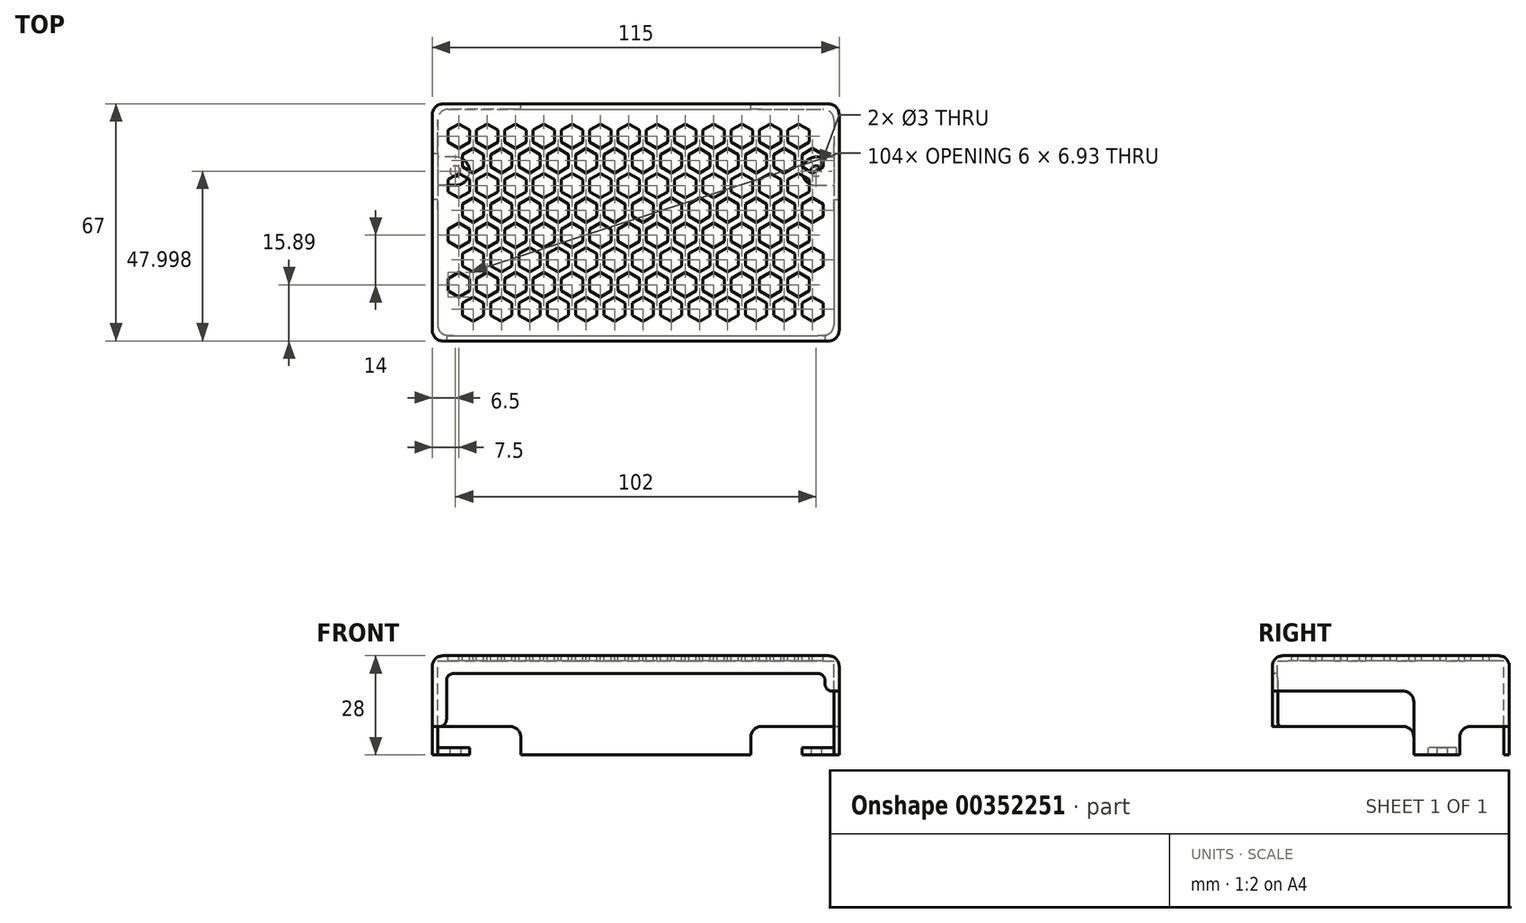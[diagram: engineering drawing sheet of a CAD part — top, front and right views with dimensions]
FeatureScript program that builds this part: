
annotation { "Feature Type Name" : "Feature", "Feature Type Description" : "" }
export const myFeature = defineFeature(function(context is Context, id is Id, definition is map)
    precondition{}
    {
        {
            var Q0;
            Q0=qCreatedBy(makeId("Top.planeOp"),FACE);
            var sketch = newSketch(context, id + "F0", { "sketchPlane" : qUnion([Q0])});
            skCircle(sketch, "E0.cCircle", {"center": v(-32, -14) * mm, "radius": 3 * mm, "construction": true});
            skLineSegment(sketch, "E0.0", {"start": v(-29, -15.73) * mm, "end": v(-32, -17.46) * mm});
            skLineSegment(sketch, "E0.1", {"start": v(-32, -17.46) * mm, "end": v(-35, -15.73) * mm});
            skLineSegment(sketch, "E0.2", {"start": v(-35, -15.73) * mm, "end": v(-35, -12.27) * mm});
            skLineSegment(sketch, "E0.3", {"start": v(-35, -12.27) * mm, "end": v(-32, -10.54) * mm});
            skLineSegment(sketch, "E0.4", {"start": v(-32, -10.54) * mm, "end": v(-29, -12.27) * mm});
            skLineSegment(sketch, "E0.5", {"start": v(-29, -12.27) * mm, "end": v(-29, -15.73) * mm});
            skPoint(sketch, "E0.0.midPoint", {"position": v(-30.5, -16.6) * mm});
            skCircle(sketch, "E1.cCircle", {"center": v(-28, -20.93) * mm, "radius": 3 * mm, "construction": true});
            skLineSegment(sketch, "E1.0", {"start": v(-25, -22.66) * mm, "end": v(-28, -24.4) * mm});
            skLineSegment(sketch, "E1.1", {"start": v(-28, -24.4) * mm, "end": v(-31, -22.66) * mm});
            skLineSegment(sketch, "E1.2", {"start": v(-31, -22.66) * mm, "end": v(-31, -19.2) * mm});
            skLineSegment(sketch, "E1.3", {"start": v(-31, -19.2) * mm, "end": v(-28, -17.46) * mm});
            skLineSegment(sketch, "E1.4", {"start": v(-28, -17.46) * mm, "end": v(-25, -19.2) * mm});
            skLineSegment(sketch, "E1.5", {"start": v(-25, -19.2) * mm, "end": v(-25, -22.66) * mm});
            skPoint(sketch, "E1.0.midPoint", {"position": v(-26.5, -23.53) * mm});
            skCircle(sketch, "E2.0.1.0", {"center": v(-28, -6.93) * mm, "radius": 3 * mm, "construction": true});
            skLineSegment(sketch, "E2.0.1.1", {"start": v(-28, -10.4) * mm, "end": v(-31, -8.66) * mm});
            skLineSegment(sketch, "E2.0.1.2", {"start": v(-31, -8.66) * mm, "end": v(-31, -5.2) * mm});
            skLineSegment(sketch, "E2.0.1.3", {"start": v(-31, -5.2) * mm, "end": v(-28, -3.46) * mm});
            skLineSegment(sketch, "E2.0.1.4", {"start": v(-28, -3.46) * mm, "end": v(-25, -5.2) * mm});
            skPoint(sketch, "E2.0.1.5", {"position": v(-26.5, -9.53) * mm});
            skPoint(sketch, "E2.0.1.6", {"position": v(-30.5, -2.6) * mm});
            skLineSegment(sketch, "E2.0.1.7", {"start": v(-25, -5.2) * mm, "end": v(-25, -8.66) * mm});
            skLineSegment(sketch, "E2.0.1.8", {"start": v(-29, 1.73) * mm, "end": v(-29, -1.73) * mm});
            skLineSegment(sketch, "E2.0.1.9", {"start": v(-32, 3.46) * mm, "end": v(-29, 1.73) * mm});
            skLineSegment(sketch, "E2.0.1.10", {"start": v(-35, 1.73) * mm, "end": v(-32, 3.46) * mm});
            skLineSegment(sketch, "E2.0.1.11", {"start": v(-35, -1.73) * mm, "end": v(-35, 1.73) * mm});
            skLineSegment(sketch, "E2.0.1.12", {"start": v(-32, -3.46) * mm, "end": v(-35, -1.73) * mm});
            skCircle(sketch, "E2.0.1.13", {"center": v(-32, 0) * mm, "radius": 3 * mm, "construction": true});
            skLineSegment(sketch, "E2.0.1.14", {"start": v(-25, -8.66) * mm, "end": v(-28, -10.4) * mm});
            skLineSegment(sketch, "E2.0.1.15", {"start": v(-29, -1.73) * mm, "end": v(-32, -3.46) * mm});
            skCircle(sketch, "E2.0.2.0", {"center": v(-28, 7.07) * mm, "radius": 3 * mm, "construction": true});
            skLineSegment(sketch, "E2.0.2.1", {"start": v(-28, 3.6) * mm, "end": v(-31, 5.34) * mm});
            skLineSegment(sketch, "E2.0.2.2", {"start": v(-31, 5.34) * mm, "end": v(-31, 8.8) * mm});
            skLineSegment(sketch, "E2.0.2.3", {"start": v(-31, 8.8) * mm, "end": v(-28, 10.54) * mm});
            skLineSegment(sketch, "E2.0.2.4", {"start": v(-28, 10.54) * mm, "end": v(-25, 8.8) * mm});
            skPoint(sketch, "E2.0.2.5", {"position": v(-26.5, 4.47) * mm});
            skPoint(sketch, "E2.0.2.6", {"position": v(-30.5, 11.4) * mm});
            skLineSegment(sketch, "E2.0.2.7", {"start": v(-25, 8.8) * mm, "end": v(-25, 5.34) * mm});
            skLineSegment(sketch, "E2.0.2.8", {"start": v(-29, 15.73) * mm, "end": v(-29, 12.27) * mm});
            skLineSegment(sketch, "E2.0.2.9", {"start": v(-32, 17.46) * mm, "end": v(-29, 15.73) * mm});
            skLineSegment(sketch, "E2.0.2.10", {"start": v(-35, 15.73) * mm, "end": v(-32, 17.46) * mm});
            skLineSegment(sketch, "E2.0.2.11", {"start": v(-35, 12.27) * mm, "end": v(-35, 15.73) * mm});
            skLineSegment(sketch, "E2.0.2.12", {"start": v(-32, 10.54) * mm, "end": v(-35, 12.27) * mm});
            skCircle(sketch, "E2.0.2.13", {"center": v(-32, 14) * mm, "radius": 3 * mm, "construction": true});
            skLineSegment(sketch, "E2.0.2.14", {"start": v(-25, 5.34) * mm, "end": v(-28, 3.6) * mm});
            skLineSegment(sketch, "E2.0.2.15", {"start": v(-29, 12.27) * mm, "end": v(-32, 10.54) * mm});
            skCircle(sketch, "E2.1.0.0", {"center": v(-20, -20.93) * mm, "radius": 3 * mm, "construction": true});
            skLineSegment(sketch, "E2.1.0.1", {"start": v(-20, -24.4) * mm, "end": v(-23, -22.66) * mm});
            skLineSegment(sketch, "E2.1.0.2", {"start": v(-23, -22.66) * mm, "end": v(-23, -19.2) * mm});
            skLineSegment(sketch, "E2.1.0.3", {"start": v(-23, -19.2) * mm, "end": v(-20, -17.46) * mm});
            skLineSegment(sketch, "E2.1.0.4", {"start": v(-20, -17.46) * mm, "end": v(-17, -19.2) * mm});
            skPoint(sketch, "E2.1.0.5", {"position": v(-18.5, -23.53) * mm});
            skPoint(sketch, "E2.1.0.6", {"position": v(-22.5, -16.6) * mm});
            skLineSegment(sketch, "E2.1.0.7", {"start": v(-17, -19.2) * mm, "end": v(-17, -22.66) * mm});
            skLineSegment(sketch, "E2.1.0.8", {"start": v(-21, -12.27) * mm, "end": v(-21, -15.73) * mm});
            skLineSegment(sketch, "E2.1.0.9", {"start": v(-24, -10.54) * mm, "end": v(-21, -12.27) * mm});
            skLineSegment(sketch, "E2.1.0.10", {"start": v(-27, -12.27) * mm, "end": v(-24, -10.54) * mm});
            skLineSegment(sketch, "E2.1.0.11", {"start": v(-27, -15.73) * mm, "end": v(-27, -12.27) * mm});
            skLineSegment(sketch, "E2.1.0.12", {"start": v(-24, -17.46) * mm, "end": v(-27, -15.73) * mm});
            skCircle(sketch, "E2.1.0.13", {"center": v(-24, -14) * mm, "radius": 3 * mm, "construction": true});
            skLineSegment(sketch, "E2.1.0.14", {"start": v(-17, -22.66) * mm, "end": v(-20, -24.4) * mm});
            skLineSegment(sketch, "E2.1.0.15", {"start": v(-21, -15.73) * mm, "end": v(-24, -17.46) * mm});
            skCircle(sketch, "E2.1.1.0", {"center": v(-20, -6.93) * mm, "radius": 3 * mm, "construction": true});
            skLineSegment(sketch, "E2.1.1.1", {"start": v(-20, -10.4) * mm, "end": v(-23, -8.66) * mm});
            skLineSegment(sketch, "E2.1.1.2", {"start": v(-23, -8.66) * mm, "end": v(-23, -5.2) * mm});
            skLineSegment(sketch, "E2.1.1.3", {"start": v(-23, -5.2) * mm, "end": v(-20, -3.46) * mm});
            skLineSegment(sketch, "E2.1.1.4", {"start": v(-20, -3.46) * mm, "end": v(-17, -5.2) * mm});
            skPoint(sketch, "E2.1.1.5", {"position": v(-18.5, -9.53) * mm});
            skPoint(sketch, "E2.1.1.6", {"position": v(-22.5, -2.6) * mm});
            skLineSegment(sketch, "E2.1.1.7", {"start": v(-17, -5.2) * mm, "end": v(-17, -8.66) * mm});
            skLineSegment(sketch, "E2.1.1.8", {"start": v(-21, 1.73) * mm, "end": v(-21, -1.73) * mm});
            skLineSegment(sketch, "E2.1.1.9", {"start": v(-24, 3.46) * mm, "end": v(-21, 1.73) * mm});
            skLineSegment(sketch, "E2.1.1.10", {"start": v(-27, 1.73) * mm, "end": v(-24, 3.46) * mm});
            skLineSegment(sketch, "E2.1.1.11", {"start": v(-27, -1.73) * mm, "end": v(-27, 1.73) * mm});
            skLineSegment(sketch, "E2.1.1.12", {"start": v(-24, -3.46) * mm, "end": v(-27, -1.73) * mm});
            skCircle(sketch, "E2.1.1.13", {"center": v(-24, 0) * mm, "radius": 3 * mm, "construction": true});
            skLineSegment(sketch, "E2.1.1.14", {"start": v(-17, -8.66) * mm, "end": v(-20, -10.4) * mm});
            skLineSegment(sketch, "E2.1.1.15", {"start": v(-21, -1.73) * mm, "end": v(-24, -3.46) * mm});
            skCircle(sketch, "E2.1.2.0", {"center": v(-20, 7.07) * mm, "radius": 3 * mm, "construction": true});
            skLineSegment(sketch, "E2.1.2.1", {"start": v(-20, 3.6) * mm, "end": v(-23, 5.34) * mm});
            skLineSegment(sketch, "E2.1.2.2", {"start": v(-23, 5.34) * mm, "end": v(-23, 8.8) * mm});
            skLineSegment(sketch, "E2.1.2.3", {"start": v(-23, 8.8) * mm, "end": v(-20, 10.54) * mm});
            skLineSegment(sketch, "E2.1.2.4", {"start": v(-20, 10.54) * mm, "end": v(-17, 8.8) * mm});
            skPoint(sketch, "E2.1.2.5", {"position": v(-18.5, 4.47) * mm});
            skPoint(sketch, "E2.1.2.6", {"position": v(-22.5, 11.4) * mm});
            skLineSegment(sketch, "E2.1.2.7", {"start": v(-17, 8.8) * mm, "end": v(-17, 5.34) * mm});
            skLineSegment(sketch, "E2.1.2.8", {"start": v(-21, 15.73) * mm, "end": v(-21, 12.27) * mm});
            skLineSegment(sketch, "E2.1.2.9", {"start": v(-24, 17.46) * mm, "end": v(-21, 15.73) * mm});
            skLineSegment(sketch, "E2.1.2.10", {"start": v(-27, 15.73) * mm, "end": v(-24, 17.46) * mm});
            skLineSegment(sketch, "E2.1.2.11", {"start": v(-27, 12.27) * mm, "end": v(-27, 15.73) * mm});
            skLineSegment(sketch, "E2.1.2.12", {"start": v(-24, 10.54) * mm, "end": v(-27, 12.27) * mm});
            skCircle(sketch, "E2.1.2.13", {"center": v(-24, 14) * mm, "radius": 3 * mm, "construction": true});
            skLineSegment(sketch, "E2.1.2.14", {"start": v(-17, 5.34) * mm, "end": v(-20, 3.6) * mm});
            skLineSegment(sketch, "E2.1.2.15", {"start": v(-21, 12.27) * mm, "end": v(-24, 10.54) * mm});
            skCircle(sketch, "E2.2.0.0", {"center": v(-12, -20.93) * mm, "radius": 3 * mm, "construction": true});
            skLineSegment(sketch, "E2.2.0.1", {"start": v(-12, -24.4) * mm, "end": v(-15, -22.66) * mm});
            skLineSegment(sketch, "E2.2.0.2", {"start": v(-15, -22.66) * mm, "end": v(-15, -19.2) * mm});
            skLineSegment(sketch, "E2.2.0.3", {"start": v(-15, -19.2) * mm, "end": v(-12, -17.46) * mm});
            skLineSegment(sketch, "E2.2.0.4", {"start": v(-12, -17.46) * mm, "end": v(-9, -19.2) * mm});
            skPoint(sketch, "E2.2.0.5", {"position": v(-10.5, -23.53) * mm});
            skPoint(sketch, "E2.2.0.6", {"position": v(-14.5, -16.6) * mm});
            skLineSegment(sketch, "E2.2.0.7", {"start": v(-9, -19.2) * mm, "end": v(-9, -22.66) * mm});
            skLineSegment(sketch, "E2.2.0.8", {"start": v(-13, -12.27) * mm, "end": v(-13, -15.73) * mm});
            skLineSegment(sketch, "E2.2.0.9", {"start": v(-16, -10.54) * mm, "end": v(-13, -12.27) * mm});
            skLineSegment(sketch, "E2.2.0.10", {"start": v(-19, -12.27) * mm, "end": v(-16, -10.54) * mm});
            skLineSegment(sketch, "E2.2.0.11", {"start": v(-19, -15.73) * mm, "end": v(-19, -12.27) * mm});
            skLineSegment(sketch, "E2.2.0.12", {"start": v(-16, -17.46) * mm, "end": v(-19, -15.73) * mm});
            skCircle(sketch, "E2.2.0.13", {"center": v(-16, -14) * mm, "radius": 3 * mm, "construction": true});
            skLineSegment(sketch, "E2.2.0.14", {"start": v(-9, -22.66) * mm, "end": v(-12, -24.4) * mm});
            skLineSegment(sketch, "E2.2.0.15", {"start": v(-13, -15.73) * mm, "end": v(-16, -17.46) * mm});
            skCircle(sketch, "E2.2.1.0", {"center": v(-12, -6.93) * mm, "radius": 3 * mm, "construction": true});
            skLineSegment(sketch, "E2.2.1.1", {"start": v(-12, -10.4) * mm, "end": v(-15, -8.66) * mm});
            skLineSegment(sketch, "E2.2.1.2", {"start": v(-15, -8.66) * mm, "end": v(-15, -5.2) * mm});
            skLineSegment(sketch, "E2.2.1.3", {"start": v(-15, -5.2) * mm, "end": v(-12, -3.46) * mm});
            skLineSegment(sketch, "E2.2.1.4", {"start": v(-12, -3.46) * mm, "end": v(-9, -5.2) * mm});
            skPoint(sketch, "E2.2.1.5", {"position": v(-10.5, -9.53) * mm});
            skPoint(sketch, "E2.2.1.6", {"position": v(-14.5, -2.6) * mm});
            skLineSegment(sketch, "E2.2.1.7", {"start": v(-9, -5.2) * mm, "end": v(-9, -8.66) * mm});
            skLineSegment(sketch, "E2.2.1.8", {"start": v(-13, 1.73) * mm, "end": v(-13, -1.73) * mm});
            skLineSegment(sketch, "E2.2.1.9", {"start": v(-16, 3.46) * mm, "end": v(-13, 1.73) * mm});
            skLineSegment(sketch, "E2.2.1.10", {"start": v(-19, 1.73) * mm, "end": v(-16, 3.46) * mm});
            skLineSegment(sketch, "E2.2.1.11", {"start": v(-19, -1.73) * mm, "end": v(-19, 1.73) * mm});
            skLineSegment(sketch, "E2.2.1.12", {"start": v(-16, -3.46) * mm, "end": v(-19, -1.73) * mm});
            skCircle(sketch, "E2.2.1.13", {"center": v(-16, 0) * mm, "radius": 3 * mm, "construction": true});
            skLineSegment(sketch, "E2.2.1.14", {"start": v(-9, -8.66) * mm, "end": v(-12, -10.4) * mm});
            skLineSegment(sketch, "E2.2.1.15", {"start": v(-13, -1.73) * mm, "end": v(-16, -3.46) * mm});
            skCircle(sketch, "E2.2.2.0", {"center": v(-12, 7.07) * mm, "radius": 3 * mm, "construction": true});
            skLineSegment(sketch, "E2.2.2.1", {"start": v(-12, 3.6) * mm, "end": v(-15, 5.34) * mm});
            skLineSegment(sketch, "E2.2.2.2", {"start": v(-15, 5.34) * mm, "end": v(-15, 8.8) * mm});
            skLineSegment(sketch, "E2.2.2.3", {"start": v(-15, 8.8) * mm, "end": v(-12, 10.54) * mm});
            skLineSegment(sketch, "E2.2.2.4", {"start": v(-12, 10.54) * mm, "end": v(-9, 8.8) * mm});
            skPoint(sketch, "E2.2.2.5", {"position": v(-10.5, 4.47) * mm});
            skPoint(sketch, "E2.2.2.6", {"position": v(-14.5, 11.4) * mm});
            skLineSegment(sketch, "E2.2.2.7", {"start": v(-9, 8.8) * mm, "end": v(-9, 5.34) * mm});
            skLineSegment(sketch, "E2.2.2.8", {"start": v(-13, 15.73) * mm, "end": v(-13, 12.27) * mm});
            skLineSegment(sketch, "E2.2.2.9", {"start": v(-16, 17.46) * mm, "end": v(-13, 15.73) * mm});
            skLineSegment(sketch, "E2.2.2.10", {"start": v(-19, 15.73) * mm, "end": v(-16, 17.46) * mm});
            skLineSegment(sketch, "E2.2.2.11", {"start": v(-19, 12.27) * mm, "end": v(-19, 15.73) * mm});
            skLineSegment(sketch, "E2.2.2.12", {"start": v(-16, 10.54) * mm, "end": v(-19, 12.27) * mm});
            skCircle(sketch, "E2.2.2.13", {"center": v(-16, 14) * mm, "radius": 3 * mm, "construction": true});
            skLineSegment(sketch, "E2.2.2.14", {"start": v(-9, 5.34) * mm, "end": v(-12, 3.6) * mm});
            skLineSegment(sketch, "E2.2.2.15", {"start": v(-13, 12.27) * mm, "end": v(-16, 10.54) * mm});
            skCircle(sketch, "E2.3.0.0", {"center": v(-4, -20.93) * mm, "radius": 3 * mm, "construction": true});
            skLineSegment(sketch, "E2.3.0.1", {"start": v(-4, -24.4) * mm, "end": v(-7, -22.66) * mm});
            skLineSegment(sketch, "E2.3.0.2", {"start": v(-7, -22.66) * mm, "end": v(-7, -19.2) * mm});
            skLineSegment(sketch, "E2.3.0.3", {"start": v(-7, -19.2) * mm, "end": v(-4, -17.46) * mm});
            skLineSegment(sketch, "E2.3.0.4", {"start": v(-4, -17.46) * mm, "end": v(-1, -19.2) * mm});
            skPoint(sketch, "E2.3.0.5", {"position": v(-2.5, -23.53) * mm});
            skPoint(sketch, "E2.3.0.6", {"position": v(-6.5, -16.6) * mm});
            skLineSegment(sketch, "E2.3.0.7", {"start": v(-1, -19.2) * mm, "end": v(-1, -22.66) * mm});
            skLineSegment(sketch, "E2.3.0.8", {"start": v(-5, -12.27) * mm, "end": v(-5, -15.73) * mm});
            skLineSegment(sketch, "E2.3.0.9", {"start": v(-8, -10.54) * mm, "end": v(-5, -12.27) * mm});
            skLineSegment(sketch, "E2.3.0.10", {"start": v(-11, -12.27) * mm, "end": v(-8, -10.54) * mm});
            skLineSegment(sketch, "E2.3.0.11", {"start": v(-11, -15.73) * mm, "end": v(-11, -12.27) * mm});
            skLineSegment(sketch, "E2.3.0.12", {"start": v(-8, -17.46) * mm, "end": v(-11, -15.73) * mm});
            skCircle(sketch, "E2.3.0.13", {"center": v(-8, -14) * mm, "radius": 3 * mm, "construction": true});
            skLineSegment(sketch, "E2.3.0.14", {"start": v(-1, -22.66) * mm, "end": v(-4, -24.4) * mm});
            skLineSegment(sketch, "E2.3.0.15", {"start": v(-5, -15.73) * mm, "end": v(-8, -17.46) * mm});
            skCircle(sketch, "E2.3.1.0", {"center": v(-4, -6.93) * mm, "radius": 3 * mm, "construction": true});
            skLineSegment(sketch, "E2.3.1.1", {"start": v(-4, -10.4) * mm, "end": v(-7, -8.66) * mm});
            skLineSegment(sketch, "E2.3.1.2", {"start": v(-7, -8.66) * mm, "end": v(-7, -5.2) * mm});
            skLineSegment(sketch, "E2.3.1.3", {"start": v(-7, -5.2) * mm, "end": v(-4, -3.46) * mm});
            skLineSegment(sketch, "E2.3.1.4", {"start": v(-4, -3.46) * mm, "end": v(-1, -5.2) * mm});
            skPoint(sketch, "E2.3.1.5", {"position": v(-2.5, -9.53) * mm});
            skPoint(sketch, "E2.3.1.6", {"position": v(-6.5, -2.6) * mm});
            skLineSegment(sketch, "E2.3.1.7", {"start": v(-1, -5.2) * mm, "end": v(-1, -8.66) * mm});
            skLineSegment(sketch, "E2.3.1.8", {"start": v(-5, 1.73) * mm, "end": v(-5, -1.73) * mm});
            skLineSegment(sketch, "E2.3.1.9", {"start": v(-8, 3.46) * mm, "end": v(-5, 1.73) * mm});
            skLineSegment(sketch, "E2.3.1.10", {"start": v(-11, 1.73) * mm, "end": v(-8, 3.46) * mm});
            skLineSegment(sketch, "E2.3.1.11", {"start": v(-11, -1.73) * mm, "end": v(-11, 1.73) * mm});
            skLineSegment(sketch, "E2.3.1.12", {"start": v(-8, -3.46) * mm, "end": v(-11, -1.73) * mm});
            skCircle(sketch, "E2.3.1.13", {"center": v(-8, 0) * mm, "radius": 3 * mm, "construction": true});
            skLineSegment(sketch, "E2.3.1.14", {"start": v(-1, -8.66) * mm, "end": v(-4, -10.4) * mm});
            skLineSegment(sketch, "E2.3.1.15", {"start": v(-5, -1.73) * mm, "end": v(-8, -3.46) * mm});
            skCircle(sketch, "E2.3.2.0", {"center": v(-4, 7.07) * mm, "radius": 3 * mm, "construction": true});
            skLineSegment(sketch, "E2.3.2.1", {"start": v(-4, 3.6) * mm, "end": v(-7, 5.34) * mm});
            skLineSegment(sketch, "E2.3.2.2", {"start": v(-7, 5.34) * mm, "end": v(-7, 8.8) * mm});
            skLineSegment(sketch, "E2.3.2.3", {"start": v(-7, 8.8) * mm, "end": v(-4, 10.54) * mm});
            skLineSegment(sketch, "E2.3.2.4", {"start": v(-4, 10.54) * mm, "end": v(-1, 8.8) * mm});
            skPoint(sketch, "E2.3.2.5", {"position": v(-2.5, 4.47) * mm});
            skPoint(sketch, "E2.3.2.6", {"position": v(-6.5, 11.4) * mm});
            skLineSegment(sketch, "E2.3.2.7", {"start": v(-1, 8.8) * mm, "end": v(-1, 5.34) * mm});
            skLineSegment(sketch, "E2.3.2.8", {"start": v(-5, 15.73) * mm, "end": v(-5, 12.27) * mm});
            skLineSegment(sketch, "E2.3.2.9", {"start": v(-8, 17.46) * mm, "end": v(-5, 15.73) * mm});
            skLineSegment(sketch, "E2.3.2.10", {"start": v(-11, 15.73) * mm, "end": v(-8, 17.46) * mm});
            skLineSegment(sketch, "E2.3.2.11", {"start": v(-11, 12.27) * mm, "end": v(-11, 15.73) * mm});
            skLineSegment(sketch, "E2.3.2.12", {"start": v(-8, 10.54) * mm, "end": v(-11, 12.27) * mm});
            skCircle(sketch, "E2.3.2.13", {"center": v(-8, 14) * mm, "radius": 3 * mm, "construction": true});
            skLineSegment(sketch, "E2.3.2.14", {"start": v(-1, 5.34) * mm, "end": v(-4, 3.6) * mm});
            skLineSegment(sketch, "E2.3.2.15", {"start": v(-5, 12.27) * mm, "end": v(-8, 10.54) * mm});
            skCircle(sketch, "E2.4.0.0", {"center": v(4, -20.93) * mm, "radius": 3 * mm, "construction": true});
            skLineSegment(sketch, "E2.4.0.1", {"start": v(4, -24.4) * mm, "end": v(1, -22.66) * mm});
            skLineSegment(sketch, "E2.4.0.2", {"start": v(1, -22.66) * mm, "end": v(1, -19.2) * mm});
            skLineSegment(sketch, "E2.4.0.3", {"start": v(1, -19.2) * mm, "end": v(4, -17.46) * mm});
            skLineSegment(sketch, "E2.4.0.4", {"start": v(4, -17.46) * mm, "end": v(7, -19.2) * mm});
            skPoint(sketch, "E2.4.0.5", {"position": v(5.5, -23.53) * mm});
            skPoint(sketch, "E2.4.0.6", {"position": v(1.5, -16.6) * mm});
            skLineSegment(sketch, "E2.4.0.7", {"start": v(7, -19.2) * mm, "end": v(7, -22.66) * mm});
            skLineSegment(sketch, "E2.4.0.8", {"start": v(3, -12.27) * mm, "end": v(3, -15.73) * mm});
            skLineSegment(sketch, "E2.4.0.9", {"start": v(0, -10.54) * mm, "end": v(3, -12.27) * mm});
            skLineSegment(sketch, "E2.4.0.10", {"start": v(-3, -12.27) * mm, "end": v(0, -10.54) * mm});
            skLineSegment(sketch, "E2.4.0.11", {"start": v(-3, -15.73) * mm, "end": v(-3, -12.27) * mm});
            skLineSegment(sketch, "E2.4.0.12", {"start": v(0, -17.46) * mm, "end": v(-3, -15.73) * mm});
            skCircle(sketch, "E2.4.0.13", {"center": v(0, -14) * mm, "radius": 3 * mm, "construction": true});
            skLineSegment(sketch, "E2.4.0.14", {"start": v(7, -22.66) * mm, "end": v(4, -24.4) * mm});
            skLineSegment(sketch, "E2.4.0.15", {"start": v(3, -15.73) * mm, "end": v(0, -17.46) * mm});
            skCircle(sketch, "E2.4.1.0", {"center": v(4, -6.93) * mm, "radius": 3 * mm, "construction": true});
            skLineSegment(sketch, "E2.4.1.1", {"start": v(4, -10.4) * mm, "end": v(1, -8.66) * mm});
            skLineSegment(sketch, "E2.4.1.2", {"start": v(1, -8.66) * mm, "end": v(1, -5.2) * mm});
            skLineSegment(sketch, "E2.4.1.3", {"start": v(1, -5.2) * mm, "end": v(4, -3.46) * mm});
            skLineSegment(sketch, "E2.4.1.4", {"start": v(4, -3.46) * mm, "end": v(7, -5.2) * mm});
            skPoint(sketch, "E2.4.1.5", {"position": v(5.5, -9.53) * mm});
            skPoint(sketch, "E2.4.1.6", {"position": v(1.5, -2.6) * mm});
            skLineSegment(sketch, "E2.4.1.7", {"start": v(7, -5.2) * mm, "end": v(7, -8.66) * mm});
            skLineSegment(sketch, "E2.4.1.8", {"start": v(3, 1.73) * mm, "end": v(3, -1.73) * mm});
            skLineSegment(sketch, "E2.4.1.9", {"start": v(0, 3.46) * mm, "end": v(3, 1.73) * mm});
            skLineSegment(sketch, "E2.4.1.10", {"start": v(-3, 1.73) * mm, "end": v(0, 3.46) * mm});
            skLineSegment(sketch, "E2.4.1.11", {"start": v(-3, -1.73) * mm, "end": v(-3, 1.73) * mm});
            skLineSegment(sketch, "E2.4.1.12", {"start": v(0, -3.46) * mm, "end": v(-3, -1.73) * mm});
            skCircle(sketch, "E2.4.1.13", {"center": v(0, 0) * mm, "radius": 3 * mm, "construction": true});
            skLineSegment(sketch, "E2.4.1.14", {"start": v(7, -8.66) * mm, "end": v(4, -10.4) * mm});
            skLineSegment(sketch, "E2.4.1.15", {"start": v(3, -1.73) * mm, "end": v(0, -3.46) * mm});
            skCircle(sketch, "E2.4.2.0", {"center": v(4, 7.07) * mm, "radius": 3 * mm, "construction": true});
            skLineSegment(sketch, "E2.4.2.1", {"start": v(4, 3.6) * mm, "end": v(1, 5.34) * mm});
            skLineSegment(sketch, "E2.4.2.2", {"start": v(1, 5.34) * mm, "end": v(1, 8.8) * mm});
            skLineSegment(sketch, "E2.4.2.3", {"start": v(1, 8.8) * mm, "end": v(4, 10.54) * mm});
            skLineSegment(sketch, "E2.4.2.4", {"start": v(4, 10.54) * mm, "end": v(7, 8.8) * mm});
            skPoint(sketch, "E2.4.2.5", {"position": v(5.5, 4.47) * mm});
            skPoint(sketch, "E2.4.2.6", {"position": v(1.5, 11.4) * mm});
            skLineSegment(sketch, "E2.4.2.7", {"start": v(7, 8.8) * mm, "end": v(7, 5.34) * mm});
            skLineSegment(sketch, "E2.4.2.8", {"start": v(3, 15.73) * mm, "end": v(3, 12.27) * mm});
            skLineSegment(sketch, "E2.4.2.9", {"start": v(0, 17.46) * mm, "end": v(3, 15.73) * mm});
            skLineSegment(sketch, "E2.4.2.10", {"start": v(-3, 15.73) * mm, "end": v(0, 17.46) * mm});
            skLineSegment(sketch, "E2.4.2.11", {"start": v(-3, 12.27) * mm, "end": v(-3, 15.73) * mm});
            skLineSegment(sketch, "E2.4.2.12", {"start": v(0, 10.54) * mm, "end": v(-3, 12.27) * mm});
            skCircle(sketch, "E2.4.2.13", {"center": v(0, 14) * mm, "radius": 3 * mm, "construction": true});
            skLineSegment(sketch, "E2.4.2.14", {"start": v(7, 5.34) * mm, "end": v(4, 3.6) * mm});
            skLineSegment(sketch, "E2.4.2.15", {"start": v(3, 12.27) * mm, "end": v(0, 10.54) * mm});
            skCircle(sketch, "E2.5.0.0", {"center": v(12, -20.93) * mm, "radius": 3 * mm, "construction": true});
            skLineSegment(sketch, "E2.5.0.1", {"start": v(12, -24.4) * mm, "end": v(9, -22.66) * mm});
            skLineSegment(sketch, "E2.5.0.2", {"start": v(9, -22.66) * mm, "end": v(9, -19.2) * mm});
            skLineSegment(sketch, "E2.5.0.3", {"start": v(9, -19.2) * mm, "end": v(12, -17.46) * mm});
            skLineSegment(sketch, "E2.5.0.4", {"start": v(12, -17.46) * mm, "end": v(15, -19.2) * mm});
            skPoint(sketch, "E2.5.0.5", {"position": v(13.5, -23.53) * mm});
            skPoint(sketch, "E2.5.0.6", {"position": v(9.5, -16.6) * mm});
            skLineSegment(sketch, "E2.5.0.7", {"start": v(15, -19.2) * mm, "end": v(15, -22.66) * mm});
            skLineSegment(sketch, "E2.5.0.8", {"start": v(11, -12.27) * mm, "end": v(11, -15.73) * mm});
            skLineSegment(sketch, "E2.5.0.9", {"start": v(8, -10.54) * mm, "end": v(11, -12.27) * mm});
            skLineSegment(sketch, "E2.5.0.10", {"start": v(5, -12.27) * mm, "end": v(8, -10.54) * mm});
            skLineSegment(sketch, "E2.5.0.11", {"start": v(5, -15.73) * mm, "end": v(5, -12.27) * mm});
            skLineSegment(sketch, "E2.5.0.12", {"start": v(8, -17.46) * mm, "end": v(5, -15.73) * mm});
            skCircle(sketch, "E2.5.0.13", {"center": v(8, -14) * mm, "radius": 3 * mm, "construction": true});
            skLineSegment(sketch, "E2.5.0.14", {"start": v(15, -22.66) * mm, "end": v(12, -24.4) * mm});
            skLineSegment(sketch, "E2.5.0.15", {"start": v(11, -15.73) * mm, "end": v(8, -17.46) * mm});
            skCircle(sketch, "E2.5.1.0", {"center": v(12, -6.93) * mm, "radius": 3 * mm, "construction": true});
            skLineSegment(sketch, "E2.5.1.1", {"start": v(12, -10.4) * mm, "end": v(9, -8.66) * mm});
            skLineSegment(sketch, "E2.5.1.2", {"start": v(9, -8.66) * mm, "end": v(9, -5.2) * mm});
            skLineSegment(sketch, "E2.5.1.3", {"start": v(9, -5.2) * mm, "end": v(12, -3.46) * mm});
            skLineSegment(sketch, "E2.5.1.4", {"start": v(12, -3.46) * mm, "end": v(15, -5.2) * mm});
            skPoint(sketch, "E2.5.1.5", {"position": v(13.5, -9.53) * mm});
            skPoint(sketch, "E2.5.1.6", {"position": v(9.5, -2.6) * mm});
            skLineSegment(sketch, "E2.5.1.7", {"start": v(15, -5.2) * mm, "end": v(15, -8.66) * mm});
            skLineSegment(sketch, "E2.5.1.8", {"start": v(11, 1.73) * mm, "end": v(11, -1.73) * mm});
            skLineSegment(sketch, "E2.5.1.9", {"start": v(8, 3.46) * mm, "end": v(11, 1.73) * mm});
            skLineSegment(sketch, "E2.5.1.10", {"start": v(5, 1.73) * mm, "end": v(8, 3.46) * mm});
            skLineSegment(sketch, "E2.5.1.11", {"start": v(5, -1.73) * mm, "end": v(5, 1.73) * mm});
            skLineSegment(sketch, "E2.5.1.12", {"start": v(8, -3.46) * mm, "end": v(5, -1.73) * mm});
            skCircle(sketch, "E2.5.1.13", {"center": v(8, 0) * mm, "radius": 3 * mm, "construction": true});
            skLineSegment(sketch, "E2.5.1.14", {"start": v(15, -8.66) * mm, "end": v(12, -10.4) * mm});
            skLineSegment(sketch, "E2.5.1.15", {"start": v(11, -1.73) * mm, "end": v(8, -3.46) * mm});
            skCircle(sketch, "E2.5.2.0", {"center": v(12, 7.07) * mm, "radius": 3 * mm, "construction": true});
            skLineSegment(sketch, "E2.5.2.1", {"start": v(12, 3.6) * mm, "end": v(9, 5.34) * mm});
            skLineSegment(sketch, "E2.5.2.2", {"start": v(9, 5.34) * mm, "end": v(9, 8.8) * mm});
            skLineSegment(sketch, "E2.5.2.3", {"start": v(9, 8.8) * mm, "end": v(12, 10.54) * mm});
            skLineSegment(sketch, "E2.5.2.4", {"start": v(12, 10.54) * mm, "end": v(15, 8.8) * mm});
            skPoint(sketch, "E2.5.2.5", {"position": v(13.5, 4.47) * mm});
            skPoint(sketch, "E2.5.2.6", {"position": v(9.5, 11.4) * mm});
            skLineSegment(sketch, "E2.5.2.7", {"start": v(15, 8.8) * mm, "end": v(15, 5.34) * mm});
            skLineSegment(sketch, "E2.5.2.8", {"start": v(11, 15.73) * mm, "end": v(11, 12.27) * mm});
            skLineSegment(sketch, "E2.5.2.9", {"start": v(8, 17.46) * mm, "end": v(11, 15.73) * mm});
            skLineSegment(sketch, "E2.5.2.10", {"start": v(5, 15.73) * mm, "end": v(8, 17.46) * mm});
            skLineSegment(sketch, "E2.5.2.11", {"start": v(5, 12.27) * mm, "end": v(5, 15.73) * mm});
            skLineSegment(sketch, "E2.5.2.12", {"start": v(8, 10.54) * mm, "end": v(5, 12.27) * mm});
            skCircle(sketch, "E2.5.2.13", {"center": v(8, 14) * mm, "radius": 3 * mm, "construction": true});
            skLineSegment(sketch, "E2.5.2.14", {"start": v(15, 5.34) * mm, "end": v(12, 3.6) * mm});
            skLineSegment(sketch, "E2.5.2.15", {"start": v(11, 12.27) * mm, "end": v(8, 10.54) * mm});
            skCircle(sketch, "E2.6.0.0", {"center": v(20, -20.93) * mm, "radius": 3 * mm, "construction": true});
            skLineSegment(sketch, "E2.6.0.1", {"start": v(20, -24.4) * mm, "end": v(17, -22.66) * mm});
            skLineSegment(sketch, "E2.6.0.2", {"start": v(17, -22.66) * mm, "end": v(17, -19.2) * mm});
            skLineSegment(sketch, "E2.6.0.3", {"start": v(17, -19.2) * mm, "end": v(20, -17.46) * mm});
            skLineSegment(sketch, "E2.6.0.4", {"start": v(20, -17.46) * mm, "end": v(23, -19.2) * mm});
            skPoint(sketch, "E2.6.0.5", {"position": v(21.5, -23.53) * mm});
            skPoint(sketch, "E2.6.0.6", {"position": v(17.5, -16.6) * mm});
            skLineSegment(sketch, "E2.6.0.7", {"start": v(23, -19.2) * mm, "end": v(23, -22.66) * mm});
            skLineSegment(sketch, "E2.6.0.8", {"start": v(19, -12.27) * mm, "end": v(19, -15.73) * mm});
            skLineSegment(sketch, "E2.6.0.9", {"start": v(16, -10.54) * mm, "end": v(19, -12.27) * mm});
            skLineSegment(sketch, "E2.6.0.10", {"start": v(13, -12.27) * mm, "end": v(16, -10.54) * mm});
            skLineSegment(sketch, "E2.6.0.11", {"start": v(13, -15.73) * mm, "end": v(13, -12.27) * mm});
            skLineSegment(sketch, "E2.6.0.12", {"start": v(16, -17.46) * mm, "end": v(13, -15.73) * mm});
            skCircle(sketch, "E2.6.0.13", {"center": v(16, -14) * mm, "radius": 3 * mm, "construction": true});
            skLineSegment(sketch, "E2.6.0.14", {"start": v(23, -22.66) * mm, "end": v(20, -24.4) * mm});
            skLineSegment(sketch, "E2.6.0.15", {"start": v(19, -15.73) * mm, "end": v(16, -17.46) * mm});
            skCircle(sketch, "E2.6.1.0", {"center": v(20, -6.93) * mm, "radius": 3 * mm, "construction": true});
            skLineSegment(sketch, "E2.6.1.1", {"start": v(20, -10.4) * mm, "end": v(17, -8.66) * mm});
            skLineSegment(sketch, "E2.6.1.2", {"start": v(17, -8.66) * mm, "end": v(17, -5.2) * mm});
            skLineSegment(sketch, "E2.6.1.3", {"start": v(17, -5.2) * mm, "end": v(20, -3.46) * mm});
            skLineSegment(sketch, "E2.6.1.4", {"start": v(20, -3.46) * mm, "end": v(23, -5.2) * mm});
            skPoint(sketch, "E2.6.1.5", {"position": v(21.5, -9.53) * mm});
            skPoint(sketch, "E2.6.1.6", {"position": v(17.5, -2.6) * mm});
            skLineSegment(sketch, "E2.6.1.7", {"start": v(23, -5.2) * mm, "end": v(23, -8.66) * mm});
            skLineSegment(sketch, "E2.6.1.8", {"start": v(19, 1.73) * mm, "end": v(19, -1.73) * mm});
            skLineSegment(sketch, "E2.6.1.9", {"start": v(16, 3.46) * mm, "end": v(19, 1.73) * mm});
            skLineSegment(sketch, "E2.6.1.10", {"start": v(13, 1.73) * mm, "end": v(16, 3.46) * mm});
            skLineSegment(sketch, "E2.6.1.11", {"start": v(13, -1.73) * mm, "end": v(13, 1.73) * mm});
            skLineSegment(sketch, "E2.6.1.12", {"start": v(16, -3.46) * mm, "end": v(13, -1.73) * mm});
            skCircle(sketch, "E2.6.1.13", {"center": v(16, 0) * mm, "radius": 3 * mm, "construction": true});
            skLineSegment(sketch, "E2.6.1.14", {"start": v(23, -8.66) * mm, "end": v(20, -10.4) * mm});
            skLineSegment(sketch, "E2.6.1.15", {"start": v(19, -1.73) * mm, "end": v(16, -3.46) * mm});
            skCircle(sketch, "E2.6.2.0", {"center": v(20, 7.07) * mm, "radius": 3 * mm, "construction": true});
            skLineSegment(sketch, "E2.6.2.1", {"start": v(20, 3.6) * mm, "end": v(17, 5.34) * mm});
            skLineSegment(sketch, "E2.6.2.2", {"start": v(17, 5.34) * mm, "end": v(17, 8.8) * mm});
            skLineSegment(sketch, "E2.6.2.3", {"start": v(17, 8.8) * mm, "end": v(20, 10.54) * mm});
            skLineSegment(sketch, "E2.6.2.4", {"start": v(20, 10.54) * mm, "end": v(23, 8.8) * mm});
            skPoint(sketch, "E2.6.2.5", {"position": v(21.5, 4.47) * mm});
            skPoint(sketch, "E2.6.2.6", {"position": v(17.5, 11.4) * mm});
            skLineSegment(sketch, "E2.6.2.7", {"start": v(23, 8.8) * mm, "end": v(23, 5.34) * mm});
            skLineSegment(sketch, "E2.6.2.8", {"start": v(19, 15.73) * mm, "end": v(19, 12.27) * mm});
            skLineSegment(sketch, "E2.6.2.9", {"start": v(16, 17.46) * mm, "end": v(19, 15.73) * mm});
            skLineSegment(sketch, "E2.6.2.10", {"start": v(13, 15.73) * mm, "end": v(16, 17.46) * mm});
            skLineSegment(sketch, "E2.6.2.11", {"start": v(13, 12.27) * mm, "end": v(13, 15.73) * mm});
            skLineSegment(sketch, "E2.6.2.12", {"start": v(16, 10.54) * mm, "end": v(13, 12.27) * mm});
            skCircle(sketch, "E2.6.2.13", {"center": v(16, 14) * mm, "radius": 3 * mm, "construction": true});
            skLineSegment(sketch, "E2.6.2.14", {"start": v(23, 5.34) * mm, "end": v(20, 3.6) * mm});
            skLineSegment(sketch, "E2.6.2.15", {"start": v(19, 12.27) * mm, "end": v(16, 10.54) * mm});
            skCircle(sketch, "E2.7.0.0", {"center": v(28, -20.93) * mm, "radius": 3 * mm, "construction": true});
            skLineSegment(sketch, "E2.7.0.1", {"start": v(28, -24.4) * mm, "end": v(25, -22.66) * mm});
            skLineSegment(sketch, "E2.7.0.2", {"start": v(25, -22.66) * mm, "end": v(25, -19.2) * mm});
            skLineSegment(sketch, "E2.7.0.3", {"start": v(25, -19.2) * mm, "end": v(28, -17.46) * mm});
            skLineSegment(sketch, "E2.7.0.4", {"start": v(28, -17.46) * mm, "end": v(31, -19.2) * mm});
            skPoint(sketch, "E2.7.0.5", {"position": v(29.5, -23.53) * mm});
            skPoint(sketch, "E2.7.0.6", {"position": v(25.5, -16.6) * mm});
            skLineSegment(sketch, "E2.7.0.7", {"start": v(31, -19.2) * mm, "end": v(31, -22.66) * mm});
            skLineSegment(sketch, "E2.7.0.8", {"start": v(27, -12.27) * mm, "end": v(27, -15.73) * mm});
            skLineSegment(sketch, "E2.7.0.9", {"start": v(24, -10.54) * mm, "end": v(27, -12.27) * mm});
            skLineSegment(sketch, "E2.7.0.10", {"start": v(21, -12.27) * mm, "end": v(24, -10.54) * mm});
            skLineSegment(sketch, "E2.7.0.11", {"start": v(21, -15.73) * mm, "end": v(21, -12.27) * mm});
            skLineSegment(sketch, "E2.7.0.12", {"start": v(24, -17.46) * mm, "end": v(21, -15.73) * mm});
            skCircle(sketch, "E2.7.0.13", {"center": v(24, -14) * mm, "radius": 3 * mm, "construction": true});
            skLineSegment(sketch, "E2.7.0.14", {"start": v(31, -22.66) * mm, "end": v(28, -24.4) * mm});
            skLineSegment(sketch, "E2.7.0.15", {"start": v(27, -15.73) * mm, "end": v(24, -17.46) * mm});
            skCircle(sketch, "E2.7.1.0", {"center": v(28, -6.93) * mm, "radius": 3 * mm, "construction": true});
            skLineSegment(sketch, "E2.7.1.1", {"start": v(28, -10.4) * mm, "end": v(25, -8.66) * mm});
            skLineSegment(sketch, "E2.7.1.2", {"start": v(25, -8.66) * mm, "end": v(25, -5.2) * mm});
            skLineSegment(sketch, "E2.7.1.3", {"start": v(25, -5.2) * mm, "end": v(28, -3.46) * mm});
            skLineSegment(sketch, "E2.7.1.4", {"start": v(28, -3.46) * mm, "end": v(31, -5.2) * mm});
            skPoint(sketch, "E2.7.1.5", {"position": v(29.5, -9.53) * mm});
            skPoint(sketch, "E2.7.1.6", {"position": v(25.5, -2.6) * mm});
            skLineSegment(sketch, "E2.7.1.7", {"start": v(31, -5.2) * mm, "end": v(31, -8.66) * mm});
            skLineSegment(sketch, "E2.7.1.8", {"start": v(27, 1.73) * mm, "end": v(27, -1.73) * mm});
            skLineSegment(sketch, "E2.7.1.9", {"start": v(24, 3.46) * mm, "end": v(27, 1.73) * mm});
            skLineSegment(sketch, "E2.7.1.10", {"start": v(21, 1.73) * mm, "end": v(24, 3.46) * mm});
            skLineSegment(sketch, "E2.7.1.11", {"start": v(21, -1.73) * mm, "end": v(21, 1.73) * mm});
            skLineSegment(sketch, "E2.7.1.12", {"start": v(24, -3.46) * mm, "end": v(21, -1.73) * mm});
            skCircle(sketch, "E2.7.1.13", {"center": v(24, 0) * mm, "radius": 3 * mm, "construction": true});
            skLineSegment(sketch, "E2.7.1.14", {"start": v(31, -8.66) * mm, "end": v(28, -10.4) * mm});
            skLineSegment(sketch, "E2.7.1.15", {"start": v(27, -1.73) * mm, "end": v(24, -3.46) * mm});
            skCircle(sketch, "E2.7.2.0", {"center": v(28, 7.07) * mm, "radius": 3 * mm, "construction": true});
            skLineSegment(sketch, "E2.7.2.1", {"start": v(28, 3.6) * mm, "end": v(25, 5.34) * mm});
            skLineSegment(sketch, "E2.7.2.2", {"start": v(25, 5.34) * mm, "end": v(25, 8.8) * mm});
            skLineSegment(sketch, "E2.7.2.3", {"start": v(25, 8.8) * mm, "end": v(28, 10.54) * mm});
            skLineSegment(sketch, "E2.7.2.4", {"start": v(28, 10.54) * mm, "end": v(31, 8.8) * mm});
            skPoint(sketch, "E2.7.2.5", {"position": v(29.5, 4.47) * mm});
            skPoint(sketch, "E2.7.2.6", {"position": v(25.5, 11.4) * mm});
            skLineSegment(sketch, "E2.7.2.7", {"start": v(31, 8.8) * mm, "end": v(31, 5.34) * mm});
            skLineSegment(sketch, "E2.7.2.8", {"start": v(27, 15.73) * mm, "end": v(27, 12.27) * mm});
            skLineSegment(sketch, "E2.7.2.9", {"start": v(24, 17.46) * mm, "end": v(27, 15.73) * mm});
            skLineSegment(sketch, "E2.7.2.10", {"start": v(21, 15.73) * mm, "end": v(24, 17.46) * mm});
            skLineSegment(sketch, "E2.7.2.11", {"start": v(21, 12.27) * mm, "end": v(21, 15.73) * mm});
            skLineSegment(sketch, "E2.7.2.12", {"start": v(24, 10.54) * mm, "end": v(21, 12.27) * mm});
            skCircle(sketch, "E2.7.2.13", {"center": v(24, 14) * mm, "radius": 3 * mm, "construction": true});
            skLineSegment(sketch, "E2.7.2.14", {"start": v(31, 5.34) * mm, "end": v(28, 3.6) * mm});
            skLineSegment(sketch, "E2.7.2.15", {"start": v(27, 12.27) * mm, "end": v(24, 10.54) * mm});
            skLineSegment(sketch, "E2.direction1", {"start": v(-31, -22.66) * mm, "end": v(-23, -22.66) * mm, "construction": true});
            skLineSegment(sketch, "E2.direction2", {"start": v(-31, -22.66) * mm, "end": v(-31, -8.66) * mm, "construction": true});
            skLineSegment(sketch, "E3.bottom", {"start": v(-38, 35.6) * mm, "end": v(74, 35.6) * mm});
            skLineSegment(sketch, "E3.top", {"start": v(-38, -28.4) * mm, "end": v(74, -28.4) * mm});
            skLineSegment(sketch, "E3.left", {"start": v(-38, 35.6) * mm, "end": v(-38, -28.4) * mm});
            skLineSegment(sketch, "E3.right", {"start": v(74, 35.6) * mm, "end": v(74, -28.4) * mm});
            skCircle(sketch, "E4.0.8.0", {"center": v(36, -20.93) * mm, "radius": 3 * mm, "construction": true});
            skLineSegment(sketch, "E4.2.8.0", {"start": v(36, -24.4) * mm, "end": v(33, -22.66) * mm});
            skLineSegment(sketch, "E4.5.8.0", {"start": v(33, -22.66) * mm, "end": v(33, -19.2) * mm});
            skLineSegment(sketch, "E4.8.8.0", {"start": v(33, -19.2) * mm, "end": v(36, -17.46) * mm});
            skLineSegment(sketch, "E4.11.8.0", {"start": v(36, -17.46) * mm, "end": v(39, -19.2) * mm});
            skPoint(sketch, "E4.14.8.0", {"position": v(37.5, -23.53) * mm});
            skPoint(sketch, "E4.15.8.0", {"position": v(33.5, -16.6) * mm});
            skLineSegment(sketch, "E4.16.8.0", {"start": v(39, -19.2) * mm, "end": v(39, -22.66) * mm});
            skLineSegment(sketch, "E4.19.8.0", {"start": v(35, -12.27) * mm, "end": v(35, -15.73) * mm});
            skLineSegment(sketch, "E4.22.8.0", {"start": v(32, -10.54) * mm, "end": v(35, -12.27) * mm});
            skLineSegment(sketch, "E4.25.8.0", {"start": v(29, -12.27) * mm, "end": v(32, -10.54) * mm});
            skLineSegment(sketch, "E4.28.8.0", {"start": v(29, -15.73) * mm, "end": v(29, -12.27) * mm});
            skLineSegment(sketch, "E4.31.8.0", {"start": v(32, -17.46) * mm, "end": v(29, -15.73) * mm});
            skCircle(sketch, "E4.34.8.0", {"center": v(32, -14) * mm, "radius": 3 * mm, "construction": true});
            skLineSegment(sketch, "E4.36.8.0", {"start": v(39, -22.66) * mm, "end": v(36, -24.4) * mm});
            skLineSegment(sketch, "E4.39.8.0", {"start": v(35, -15.73) * mm, "end": v(32, -17.46) * mm});
            skCircle(sketch, "E4.0.8.1", {"center": v(36, -6.93) * mm, "radius": 3 * mm, "construction": true});
            skLineSegment(sketch, "E4.2.8.1", {"start": v(36, -10.4) * mm, "end": v(33, -8.66) * mm});
            skLineSegment(sketch, "E4.5.8.1", {"start": v(33, -8.66) * mm, "end": v(33, -5.2) * mm});
            skLineSegment(sketch, "E4.8.8.1", {"start": v(33, -5.2) * mm, "end": v(36, -3.46) * mm});
            skLineSegment(sketch, "E4.11.8.1", {"start": v(36, -3.46) * mm, "end": v(39, -5.2) * mm});
            skPoint(sketch, "E4.14.8.1", {"position": v(37.5, -9.53) * mm});
            skPoint(sketch, "E4.15.8.1", {"position": v(33.5, -2.6) * mm});
            skLineSegment(sketch, "E4.16.8.1", {"start": v(39, -5.2) * mm, "end": v(39, -8.66) * mm});
            skLineSegment(sketch, "E4.19.8.1", {"start": v(35, 1.73) * mm, "end": v(35, -1.73) * mm});
            skLineSegment(sketch, "E4.22.8.1", {"start": v(32, 3.46) * mm, "end": v(35, 1.73) * mm});
            skLineSegment(sketch, "E4.25.8.1", {"start": v(29, 1.73) * mm, "end": v(32, 3.46) * mm});
            skLineSegment(sketch, "E4.28.8.1", {"start": v(29, -1.73) * mm, "end": v(29, 1.73) * mm});
            skLineSegment(sketch, "E4.31.8.1", {"start": v(32, -3.46) * mm, "end": v(29, -1.73) * mm});
            skCircle(sketch, "E4.34.8.1", {"center": v(32, 0) * mm, "radius": 3 * mm, "construction": true});
            skLineSegment(sketch, "E4.36.8.1", {"start": v(39, -8.66) * mm, "end": v(36, -10.4) * mm});
            skLineSegment(sketch, "E4.39.8.1", {"start": v(35, -1.73) * mm, "end": v(32, -3.46) * mm});
            skCircle(sketch, "E4.0.8.2", {"center": v(36, 7.07) * mm, "radius": 3 * mm, "construction": true});
            skLineSegment(sketch, "E4.2.8.2", {"start": v(36, 3.6) * mm, "end": v(33, 5.34) * mm});
            skLineSegment(sketch, "E4.5.8.2", {"start": v(33, 5.34) * mm, "end": v(33, 8.8) * mm});
            skLineSegment(sketch, "E4.8.8.2", {"start": v(33, 8.8) * mm, "end": v(36, 10.54) * mm});
            skLineSegment(sketch, "E4.11.8.2", {"start": v(36, 10.54) * mm, "end": v(39, 8.8) * mm});
            skPoint(sketch, "E4.14.8.2", {"position": v(37.5, 4.47) * mm});
            skPoint(sketch, "E4.15.8.2", {"position": v(33.5, 11.4) * mm});
            skLineSegment(sketch, "E4.16.8.2", {"start": v(39, 8.8) * mm, "end": v(39, 5.34) * mm});
            skLineSegment(sketch, "E4.19.8.2", {"start": v(35, 15.73) * mm, "end": v(35, 12.27) * mm});
            skLineSegment(sketch, "E4.22.8.2", {"start": v(32, 17.46) * mm, "end": v(35, 15.73) * mm});
            skLineSegment(sketch, "E4.25.8.2", {"start": v(29, 15.73) * mm, "end": v(32, 17.46) * mm});
            skLineSegment(sketch, "E4.28.8.2", {"start": v(29, 12.27) * mm, "end": v(29, 15.73) * mm});
            skLineSegment(sketch, "E4.31.8.2", {"start": v(32, 10.54) * mm, "end": v(29, 12.27) * mm});
            skCircle(sketch, "E4.34.8.2", {"center": v(32, 14) * mm, "radius": 3 * mm, "construction": true});
            skLineSegment(sketch, "E4.36.8.2", {"start": v(39, 5.34) * mm, "end": v(36, 3.6) * mm});
            skLineSegment(sketch, "E4.39.8.2", {"start": v(35, 12.27) * mm, "end": v(32, 10.54) * mm});
            skCircle(sketch, "E4.0.9.0", {"center": v(44, -20.93) * mm, "radius": 3 * mm, "construction": true});
            skLineSegment(sketch, "E4.2.9.0", {"start": v(44, -24.4) * mm, "end": v(41, -22.66) * mm});
            skLineSegment(sketch, "E4.5.9.0", {"start": v(41, -22.66) * mm, "end": v(41, -19.2) * mm});
            skLineSegment(sketch, "E4.8.9.0", {"start": v(41, -19.2) * mm, "end": v(44, -17.46) * mm});
            skLineSegment(sketch, "E4.11.9.0", {"start": v(44, -17.46) * mm, "end": v(47, -19.2) * mm});
            skPoint(sketch, "E4.14.9.0", {"position": v(45.5, -23.53) * mm});
            skPoint(sketch, "E4.15.9.0", {"position": v(41.5, -16.6) * mm});
            skLineSegment(sketch, "E4.16.9.0", {"start": v(47, -19.2) * mm, "end": v(47, -22.66) * mm});
            skLineSegment(sketch, "E4.19.9.0", {"start": v(43, -12.27) * mm, "end": v(43, -15.73) * mm});
            skLineSegment(sketch, "E4.22.9.0", {"start": v(40, -10.54) * mm, "end": v(43, -12.27) * mm});
            skLineSegment(sketch, "E4.25.9.0", {"start": v(37, -12.27) * mm, "end": v(40, -10.54) * mm});
            skLineSegment(sketch, "E4.28.9.0", {"start": v(37, -15.73) * mm, "end": v(37, -12.27) * mm});
            skLineSegment(sketch, "E4.31.9.0", {"start": v(40, -17.46) * mm, "end": v(37, -15.73) * mm});
            skCircle(sketch, "E4.34.9.0", {"center": v(40, -14) * mm, "radius": 3 * mm, "construction": true});
            skLineSegment(sketch, "E4.36.9.0", {"start": v(47, -22.66) * mm, "end": v(44, -24.4) * mm});
            skLineSegment(sketch, "E4.39.9.0", {"start": v(43, -15.73) * mm, "end": v(40, -17.46) * mm});
            skCircle(sketch, "E4.0.9.1", {"center": v(44, -6.93) * mm, "radius": 3 * mm, "construction": true});
            skLineSegment(sketch, "E4.2.9.1", {"start": v(44, -10.4) * mm, "end": v(41, -8.66) * mm});
            skLineSegment(sketch, "E4.5.9.1", {"start": v(41, -8.66) * mm, "end": v(41, -5.2) * mm});
            skLineSegment(sketch, "E4.8.9.1", {"start": v(41, -5.2) * mm, "end": v(44, -3.46) * mm});
            skLineSegment(sketch, "E4.11.9.1", {"start": v(44, -3.46) * mm, "end": v(47, -5.2) * mm});
            skPoint(sketch, "E4.14.9.1", {"position": v(45.5, -9.53) * mm});
            skPoint(sketch, "E4.15.9.1", {"position": v(41.5, -2.6) * mm});
            skLineSegment(sketch, "E4.16.9.1", {"start": v(47, -5.2) * mm, "end": v(47, -8.66) * mm});
            skLineSegment(sketch, "E4.19.9.1", {"start": v(43, 1.73) * mm, "end": v(43, -1.73) * mm});
            skLineSegment(sketch, "E4.22.9.1", {"start": v(40, 3.46) * mm, "end": v(43, 1.73) * mm});
            skLineSegment(sketch, "E4.25.9.1", {"start": v(37, 1.73) * mm, "end": v(40, 3.46) * mm});
            skLineSegment(sketch, "E4.28.9.1", {"start": v(37, -1.73) * mm, "end": v(37, 1.73) * mm});
            skLineSegment(sketch, "E4.31.9.1", {"start": v(40, -3.46) * mm, "end": v(37, -1.73) * mm});
            skCircle(sketch, "E4.34.9.1", {"center": v(40, 0) * mm, "radius": 3 * mm, "construction": true});
            skLineSegment(sketch, "E4.36.9.1", {"start": v(47, -8.66) * mm, "end": v(44, -10.4) * mm});
            skLineSegment(sketch, "E4.39.9.1", {"start": v(43, -1.73) * mm, "end": v(40, -3.46) * mm});
            skCircle(sketch, "E4.0.9.2", {"center": v(44, 7.07) * mm, "radius": 3 * mm, "construction": true});
            skLineSegment(sketch, "E4.2.9.2", {"start": v(44, 3.6) * mm, "end": v(41, 5.34) * mm});
            skLineSegment(sketch, "E4.5.9.2", {"start": v(41, 5.34) * mm, "end": v(41, 8.8) * mm});
            skLineSegment(sketch, "E4.8.9.2", {"start": v(41, 8.8) * mm, "end": v(44, 10.54) * mm});
            skLineSegment(sketch, "E4.11.9.2", {"start": v(44, 10.54) * mm, "end": v(47, 8.8) * mm});
            skPoint(sketch, "E4.14.9.2", {"position": v(45.5, 4.47) * mm});
            skPoint(sketch, "E4.15.9.2", {"position": v(41.5, 11.4) * mm});
            skLineSegment(sketch, "E4.16.9.2", {"start": v(47, 8.8) * mm, "end": v(47, 5.34) * mm});
            skLineSegment(sketch, "E4.19.9.2", {"start": v(43, 15.73) * mm, "end": v(43, 12.27) * mm});
            skLineSegment(sketch, "E4.22.9.2", {"start": v(40, 17.46) * mm, "end": v(43, 15.73) * mm});
            skLineSegment(sketch, "E4.25.9.2", {"start": v(37, 15.73) * mm, "end": v(40, 17.46) * mm});
            skLineSegment(sketch, "E4.28.9.2", {"start": v(37, 12.27) * mm, "end": v(37, 15.73) * mm});
            skLineSegment(sketch, "E4.31.9.2", {"start": v(40, 10.54) * mm, "end": v(37, 12.27) * mm});
            skCircle(sketch, "E4.34.9.2", {"center": v(40, 14) * mm, "radius": 3 * mm, "construction": true});
            skLineSegment(sketch, "E4.36.9.2", {"start": v(47, 5.34) * mm, "end": v(44, 3.6) * mm});
            skLineSegment(sketch, "E4.39.9.2", {"start": v(43, 12.27) * mm, "end": v(40, 10.54) * mm});
            skCircle(sketch, "E5.0.10.0", {"center": v(52, -20.93) * mm, "radius": 3 * mm, "construction": true});
            skLineSegment(sketch, "E5.2.10.0", {"start": v(52, -24.4) * mm, "end": v(49, -22.66) * mm});
            skLineSegment(sketch, "E5.5.10.0", {"start": v(49, -22.66) * mm, "end": v(49, -19.2) * mm});
            skLineSegment(sketch, "E5.8.10.0", {"start": v(49, -19.2) * mm, "end": v(52, -17.46) * mm});
            skLineSegment(sketch, "E5.11.10.0", {"start": v(52, -17.46) * mm, "end": v(55, -19.2) * mm});
            skPoint(sketch, "E5.14.10.0", {"position": v(53.5, -23.53) * mm});
            skPoint(sketch, "E5.15.10.0", {"position": v(49.5, -16.6) * mm});
            skLineSegment(sketch, "E5.16.10.0", {"start": v(55, -19.2) * mm, "end": v(55, -22.66) * mm});
            skLineSegment(sketch, "E5.19.10.0", {"start": v(51, -12.27) * mm, "end": v(51, -15.73) * mm});
            skLineSegment(sketch, "E5.22.10.0", {"start": v(48, -10.54) * mm, "end": v(51, -12.27) * mm});
            skLineSegment(sketch, "E5.25.10.0", {"start": v(45, -12.27) * mm, "end": v(48, -10.54) * mm});
            skLineSegment(sketch, "E5.28.10.0", {"start": v(45, -15.73) * mm, "end": v(45, -12.27) * mm});
            skLineSegment(sketch, "E5.31.10.0", {"start": v(48, -17.46) * mm, "end": v(45, -15.73) * mm});
            skCircle(sketch, "E5.34.10.0", {"center": v(48, -14) * mm, "radius": 3 * mm, "construction": true});
            skLineSegment(sketch, "E5.36.10.0", {"start": v(55, -22.66) * mm, "end": v(52, -24.4) * mm});
            skLineSegment(sketch, "E5.39.10.0", {"start": v(51, -15.73) * mm, "end": v(48, -17.46) * mm});
            skCircle(sketch, "E5.0.10.1", {"center": v(52, -6.93) * mm, "radius": 3 * mm, "construction": true});
            skLineSegment(sketch, "E5.2.10.1", {"start": v(52, -10.4) * mm, "end": v(49, -8.66) * mm});
            skLineSegment(sketch, "E5.5.10.1", {"start": v(49, -8.66) * mm, "end": v(49, -5.2) * mm});
            skLineSegment(sketch, "E5.8.10.1", {"start": v(49, -5.2) * mm, "end": v(52, -3.46) * mm});
            skLineSegment(sketch, "E5.11.10.1", {"start": v(52, -3.46) * mm, "end": v(55, -5.2) * mm});
            skPoint(sketch, "E5.14.10.1", {"position": v(53.5, -9.53) * mm});
            skPoint(sketch, "E5.15.10.1", {"position": v(49.5, -2.6) * mm});
            skLineSegment(sketch, "E5.16.10.1", {"start": v(55, -5.2) * mm, "end": v(55, -8.66) * mm});
            skLineSegment(sketch, "E5.19.10.1", {"start": v(51, 1.73) * mm, "end": v(51, -1.73) * mm});
            skLineSegment(sketch, "E5.22.10.1", {"start": v(48, 3.46) * mm, "end": v(51, 1.73) * mm});
            skLineSegment(sketch, "E5.25.10.1", {"start": v(45, 1.73) * mm, "end": v(48, 3.46) * mm});
            skLineSegment(sketch, "E5.28.10.1", {"start": v(45, -1.73) * mm, "end": v(45, 1.73) * mm});
            skLineSegment(sketch, "E5.31.10.1", {"start": v(48, -3.46) * mm, "end": v(45, -1.73) * mm});
            skCircle(sketch, "E5.34.10.1", {"center": v(48, 0) * mm, "radius": 3 * mm, "construction": true});
            skLineSegment(sketch, "E5.36.10.1", {"start": v(55, -8.66) * mm, "end": v(52, -10.4) * mm});
            skLineSegment(sketch, "E5.39.10.1", {"start": v(51, -1.73) * mm, "end": v(48, -3.46) * mm});
            skCircle(sketch, "E5.0.10.2", {"center": v(52, 7.07) * mm, "radius": 3 * mm, "construction": true});
            skLineSegment(sketch, "E5.2.10.2", {"start": v(52, 3.6) * mm, "end": v(49, 5.34) * mm});
            skLineSegment(sketch, "E5.5.10.2", {"start": v(49, 5.34) * mm, "end": v(49, 8.8) * mm});
            skLineSegment(sketch, "E5.8.10.2", {"start": v(49, 8.8) * mm, "end": v(52, 10.54) * mm});
            skLineSegment(sketch, "E5.11.10.2", {"start": v(52, 10.54) * mm, "end": v(55, 8.8) * mm});
            skPoint(sketch, "E5.14.10.2", {"position": v(53.5, 4.47) * mm});
            skPoint(sketch, "E5.15.10.2", {"position": v(49.5, 11.4) * mm});
            skLineSegment(sketch, "E5.16.10.2", {"start": v(55, 8.8) * mm, "end": v(55, 5.34) * mm});
            skLineSegment(sketch, "E5.19.10.2", {"start": v(51, 15.73) * mm, "end": v(51, 12.27) * mm});
            skLineSegment(sketch, "E5.22.10.2", {"start": v(48, 17.46) * mm, "end": v(51, 15.73) * mm});
            skLineSegment(sketch, "E5.25.10.2", {"start": v(45, 15.73) * mm, "end": v(48, 17.46) * mm});
            skLineSegment(sketch, "E5.28.10.2", {"start": v(45, 12.27) * mm, "end": v(45, 15.73) * mm});
            skLineSegment(sketch, "E5.31.10.2", {"start": v(48, 10.54) * mm, "end": v(45, 12.27) * mm});
            skCircle(sketch, "E5.34.10.2", {"center": v(48, 14) * mm, "radius": 3 * mm, "construction": true});
            skLineSegment(sketch, "E5.36.10.2", {"start": v(55, 5.34) * mm, "end": v(52, 3.6) * mm});
            skLineSegment(sketch, "E5.39.10.2", {"start": v(51, 12.27) * mm, "end": v(48, 10.54) * mm});
            skLineSegment(sketch, "E6.bottom", {"start": v(-39.5, 37.1) * mm, "end": v(75.5, 37.1) * mm});
            skLineSegment(sketch, "E6.top", {"start": v(-39.5, -29.9) * mm, "end": v(75.5, -29.9) * mm});
            skLineSegment(sketch, "E6.left", {"start": v(-39.5, 37.1) * mm, "end": v(-39.5, -29.9) * mm});
            skLineSegment(sketch, "E6.right", {"start": v(75.5, 37.1) * mm, "end": v(75.5, -29.9) * mm});
            skCircle(sketch, "E7.0.11.0", {"center": v(60, -20.93) * mm, "radius": 3 * mm, "construction": true});
            skLineSegment(sketch, "E7.2.11.0", {"start": v(60, -24.4) * mm, "end": v(57, -22.66) * mm});
            skLineSegment(sketch, "E7.5.11.0", {"start": v(57, -22.66) * mm, "end": v(57, -19.2) * mm});
            skLineSegment(sketch, "E7.8.11.0", {"start": v(57, -19.2) * mm, "end": v(60, -17.46) * mm});
            skLineSegment(sketch, "E7.11.11.0", {"start": v(60, -17.46) * mm, "end": v(63, -19.2) * mm});
            skPoint(sketch, "E7.14.11.0", {"position": v(61.5, -23.53) * mm});
            skPoint(sketch, "E7.15.11.0", {"position": v(57.5, -16.6) * mm});
            skLineSegment(sketch, "E7.16.11.0", {"start": v(63, -19.2) * mm, "end": v(63, -22.66) * mm});
            skLineSegment(sketch, "E7.19.11.0", {"start": v(59, -12.27) * mm, "end": v(59, -15.73) * mm});
            skLineSegment(sketch, "E7.22.11.0", {"start": v(56, -10.54) * mm, "end": v(59, -12.27) * mm});
            skLineSegment(sketch, "E7.25.11.0", {"start": v(53, -12.27) * mm, "end": v(56, -10.54) * mm});
            skLineSegment(sketch, "E7.28.11.0", {"start": v(53, -15.73) * mm, "end": v(53, -12.27) * mm});
            skLineSegment(sketch, "E7.31.11.0", {"start": v(56, -17.46) * mm, "end": v(53, -15.73) * mm});
            skCircle(sketch, "E7.34.11.0", {"center": v(56, -14) * mm, "radius": 3 * mm, "construction": true});
            skLineSegment(sketch, "E7.36.11.0", {"start": v(63, -22.66) * mm, "end": v(60, -24.4) * mm});
            skLineSegment(sketch, "E7.39.11.0", {"start": v(59, -15.73) * mm, "end": v(56, -17.46) * mm});
            skCircle(sketch, "E7.0.11.1", {"center": v(60, -6.93) * mm, "radius": 3 * mm, "construction": true});
            skLineSegment(sketch, "E7.2.11.1", {"start": v(60, -10.4) * mm, "end": v(57, -8.66) * mm});
            skLineSegment(sketch, "E7.5.11.1", {"start": v(57, -8.66) * mm, "end": v(57, -5.2) * mm});
            skLineSegment(sketch, "E7.8.11.1", {"start": v(57, -5.2) * mm, "end": v(60, -3.46) * mm});
            skLineSegment(sketch, "E7.11.11.1", {"start": v(60, -3.46) * mm, "end": v(63, -5.2) * mm});
            skPoint(sketch, "E7.14.11.1", {"position": v(61.5, -9.53) * mm});
            skPoint(sketch, "E7.15.11.1", {"position": v(57.5, -2.6) * mm});
            skLineSegment(sketch, "E7.16.11.1", {"start": v(63, -5.2) * mm, "end": v(63, -8.66) * mm});
            skLineSegment(sketch, "E7.19.11.1", {"start": v(59, 1.73) * mm, "end": v(59, -1.73) * mm});
            skLineSegment(sketch, "E7.22.11.1", {"start": v(56, 3.46) * mm, "end": v(59, 1.73) * mm});
            skLineSegment(sketch, "E7.25.11.1", {"start": v(53, 1.73) * mm, "end": v(56, 3.46) * mm});
            skLineSegment(sketch, "E7.28.11.1", {"start": v(53, -1.73) * mm, "end": v(53, 1.73) * mm});
            skLineSegment(sketch, "E7.31.11.1", {"start": v(56, -3.46) * mm, "end": v(53, -1.73) * mm});
            skCircle(sketch, "E7.34.11.1", {"center": v(56, 0) * mm, "radius": 3 * mm, "construction": true});
            skLineSegment(sketch, "E7.36.11.1", {"start": v(63, -8.66) * mm, "end": v(60, -10.4) * mm});
            skLineSegment(sketch, "E7.39.11.1", {"start": v(59, -1.73) * mm, "end": v(56, -3.46) * mm});
            skCircle(sketch, "E7.0.11.2", {"center": v(60, 7.07) * mm, "radius": 3 * mm, "construction": true});
            skLineSegment(sketch, "E7.2.11.2", {"start": v(60, 3.6) * mm, "end": v(57, 5.34) * mm});
            skLineSegment(sketch, "E7.5.11.2", {"start": v(57, 5.34) * mm, "end": v(57, 8.8) * mm});
            skLineSegment(sketch, "E7.8.11.2", {"start": v(57, 8.8) * mm, "end": v(60, 10.54) * mm});
            skLineSegment(sketch, "E7.11.11.2", {"start": v(60, 10.54) * mm, "end": v(63, 8.8) * mm});
            skPoint(sketch, "E7.14.11.2", {"position": v(61.5, 4.47) * mm});
            skPoint(sketch, "E7.15.11.2", {"position": v(57.5, 11.4) * mm});
            skLineSegment(sketch, "E7.16.11.2", {"start": v(63, 8.8) * mm, "end": v(63, 5.34) * mm});
            skLineSegment(sketch, "E7.19.11.2", {"start": v(59, 15.73) * mm, "end": v(59, 12.27) * mm});
            skLineSegment(sketch, "E7.22.11.2", {"start": v(56, 17.46) * mm, "end": v(59, 15.73) * mm});
            skLineSegment(sketch, "E7.25.11.2", {"start": v(53, 15.73) * mm, "end": v(56, 17.46) * mm});
            skLineSegment(sketch, "E7.28.11.2", {"start": v(53, 12.27) * mm, "end": v(53, 15.73) * mm});
            skLineSegment(sketch, "E7.31.11.2", {"start": v(56, 10.54) * mm, "end": v(53, 12.27) * mm});
            skCircle(sketch, "E7.34.11.2", {"center": v(56, 14) * mm, "radius": 3 * mm, "construction": true});
            skLineSegment(sketch, "E7.36.11.2", {"start": v(63, 5.34) * mm, "end": v(60, 3.6) * mm});
            skLineSegment(sketch, "E7.39.11.2", {"start": v(59, 12.27) * mm, "end": v(56, 10.54) * mm});
            skCircle(sketch, "E8.0.12.0", {"center": v(68, -20.93) * mm, "radius": 3 * mm, "construction": true});
            skLineSegment(sketch, "E8.2.12.0", {"start": v(68, -24.4) * mm, "end": v(65, -22.66) * mm});
            skLineSegment(sketch, "E8.5.12.0", {"start": v(65, -22.66) * mm, "end": v(65, -19.2) * mm});
            skLineSegment(sketch, "E8.8.12.0", {"start": v(65, -19.2) * mm, "end": v(68, -17.46) * mm});
            skLineSegment(sketch, "E8.11.12.0", {"start": v(68, -17.46) * mm, "end": v(71, -19.2) * mm});
            skPoint(sketch, "E8.14.12.0", {"position": v(69.5, -23.53) * mm});
            skPoint(sketch, "E8.15.12.0", {"position": v(65.5, -16.6) * mm});
            skLineSegment(sketch, "E8.16.12.0", {"start": v(71, -19.2) * mm, "end": v(71, -22.66) * mm});
            skLineSegment(sketch, "E8.19.12.0", {"start": v(67, -12.27) * mm, "end": v(67, -15.73) * mm});
            skLineSegment(sketch, "E8.22.12.0", {"start": v(64, -10.54) * mm, "end": v(67, -12.27) * mm});
            skLineSegment(sketch, "E8.25.12.0", {"start": v(61, -12.27) * mm, "end": v(64, -10.54) * mm});
            skLineSegment(sketch, "E8.28.12.0", {"start": v(61, -15.73) * mm, "end": v(61, -12.27) * mm});
            skLineSegment(sketch, "E8.31.12.0", {"start": v(64, -17.46) * mm, "end": v(61, -15.73) * mm});
            skCircle(sketch, "E8.34.12.0", {"center": v(64, -14) * mm, "radius": 3 * mm, "construction": true});
            skLineSegment(sketch, "E8.36.12.0", {"start": v(71, -22.66) * mm, "end": v(68, -24.4) * mm});
            skLineSegment(sketch, "E8.39.12.0", {"start": v(67, -15.73) * mm, "end": v(64, -17.46) * mm});
            skCircle(sketch, "E8.0.12.1", {"center": v(68, -6.93) * mm, "radius": 3 * mm, "construction": true});
            skLineSegment(sketch, "E8.2.12.1", {"start": v(68, -10.4) * mm, "end": v(65, -8.66) * mm});
            skLineSegment(sketch, "E8.5.12.1", {"start": v(65, -8.66) * mm, "end": v(65, -5.2) * mm});
            skLineSegment(sketch, "E8.8.12.1", {"start": v(65, -5.2) * mm, "end": v(68, -3.46) * mm});
            skLineSegment(sketch, "E8.11.12.1", {"start": v(68, -3.46) * mm, "end": v(71, -5.2) * mm});
            skPoint(sketch, "E8.14.12.1", {"position": v(69.5, -9.53) * mm});
            skPoint(sketch, "E8.15.12.1", {"position": v(65.5, -2.6) * mm});
            skLineSegment(sketch, "E8.16.12.1", {"start": v(71, -5.2) * mm, "end": v(71, -8.66) * mm});
            skLineSegment(sketch, "E8.19.12.1", {"start": v(67, 1.73) * mm, "end": v(67, -1.73) * mm});
            skLineSegment(sketch, "E8.22.12.1", {"start": v(64, 3.46) * mm, "end": v(67, 1.73) * mm});
            skLineSegment(sketch, "E8.25.12.1", {"start": v(61, 1.73) * mm, "end": v(64, 3.46) * mm});
            skLineSegment(sketch, "E8.28.12.1", {"start": v(61, -1.73) * mm, "end": v(61, 1.73) * mm});
            skLineSegment(sketch, "E8.31.12.1", {"start": v(64, -3.46) * mm, "end": v(61, -1.73) * mm});
            skCircle(sketch, "E8.34.12.1", {"center": v(64, 0) * mm, "radius": 3 * mm, "construction": true});
            skLineSegment(sketch, "E8.36.12.1", {"start": v(71, -8.66) * mm, "end": v(68, -10.4) * mm});
            skLineSegment(sketch, "E8.39.12.1", {"start": v(67, -1.73) * mm, "end": v(64, -3.46) * mm});
            skCircle(sketch, "E8.0.12.2", {"center": v(68, 7.07) * mm, "radius": 3 * mm, "construction": true});
            skLineSegment(sketch, "E8.2.12.2", {"start": v(68, 3.6) * mm, "end": v(65, 5.34) * mm});
            skLineSegment(sketch, "E8.5.12.2", {"start": v(65, 5.34) * mm, "end": v(65, 8.8) * mm});
            skLineSegment(sketch, "E8.8.12.2", {"start": v(65, 8.8) * mm, "end": v(68, 10.54) * mm});
            skLineSegment(sketch, "E8.11.12.2", {"start": v(68, 10.54) * mm, "end": v(71, 8.8) * mm});
            skPoint(sketch, "E8.14.12.2", {"position": v(69.5, 4.47) * mm});
            skPoint(sketch, "E8.15.12.2", {"position": v(65.5, 11.4) * mm});
            skLineSegment(sketch, "E8.16.12.2", {"start": v(71, 8.8) * mm, "end": v(71, 5.34) * mm});
            skLineSegment(sketch, "E8.19.12.2", {"start": v(67, 15.73) * mm, "end": v(67, 12.27) * mm});
            skLineSegment(sketch, "E8.22.12.2", {"start": v(64, 17.46) * mm, "end": v(67, 15.73) * mm});
            skLineSegment(sketch, "E8.25.12.2", {"start": v(61, 15.73) * mm, "end": v(64, 17.46) * mm});
            skLineSegment(sketch, "E8.28.12.2", {"start": v(61, 12.27) * mm, "end": v(61, 15.73) * mm});
            skLineSegment(sketch, "E8.31.12.2", {"start": v(64, 10.54) * mm, "end": v(61, 12.27) * mm});
            skCircle(sketch, "E8.34.12.2", {"center": v(64, 14) * mm, "radius": 3 * mm, "construction": true});
            skLineSegment(sketch, "E8.36.12.2", {"start": v(71, 5.34) * mm, "end": v(68, 3.6) * mm});
            skLineSegment(sketch, "E8.39.12.2", {"start": v(67, 12.27) * mm, "end": v(64, 10.54) * mm});
            skCircle(sketch, "E9.0.0.3", {"center": v(-28, 21.07) * mm, "radius": 3 * mm, "construction": true});
            skLineSegment(sketch, "E9.2.0.3", {"start": v(-28, 17.6) * mm, "end": v(-31, 19.34) * mm});
            skLineSegment(sketch, "E9.5.0.3", {"start": v(-31, 19.34) * mm, "end": v(-31, 22.8) * mm});
            skLineSegment(sketch, "E9.8.0.3", {"start": v(-31, 22.8) * mm, "end": v(-28, 24.54) * mm});
            skLineSegment(sketch, "E9.11.0.3", {"start": v(-28, 24.54) * mm, "end": v(-25, 22.8) * mm});
            skPoint(sketch, "E9.14.0.3", {"position": v(-26.5, 18.47) * mm});
            skPoint(sketch, "E9.15.0.3", {"position": v(-30.5, 25.4) * mm});
            skLineSegment(sketch, "E9.16.0.3", {"start": v(-25, 22.8) * mm, "end": v(-25, 19.34) * mm});
            skLineSegment(sketch, "E9.19.0.3", {"start": v(-29, 29.73) * mm, "end": v(-29, 26.27) * mm});
            skLineSegment(sketch, "E9.22.0.3", {"start": v(-32, 31.46) * mm, "end": v(-29, 29.73) * mm});
            skLineSegment(sketch, "E9.25.0.3", {"start": v(-35, 29.73) * mm, "end": v(-32, 31.46) * mm});
            skLineSegment(sketch, "E9.28.0.3", {"start": v(-35, 26.27) * mm, "end": v(-35, 29.73) * mm});
            skLineSegment(sketch, "E9.31.0.3", {"start": v(-32, 24.54) * mm, "end": v(-35, 26.27) * mm});
            skCircle(sketch, "E9.34.0.3", {"center": v(-32, 28) * mm, "radius": 3 * mm, "construction": true});
            skLineSegment(sketch, "E9.36.0.3", {"start": v(-25, 19.34) * mm, "end": v(-28, 17.6) * mm});
            skLineSegment(sketch, "E9.39.0.3", {"start": v(-29, 26.27) * mm, "end": v(-32, 24.54) * mm});
            skCircle(sketch, "E9.0.1.3", {"center": v(-20, 21.07) * mm, "radius": 3 * mm, "construction": true});
            skLineSegment(sketch, "E9.2.1.3", {"start": v(-20, 17.6) * mm, "end": v(-23, 19.34) * mm});
            skLineSegment(sketch, "E9.5.1.3", {"start": v(-23, 19.34) * mm, "end": v(-23, 22.8) * mm});
            skLineSegment(sketch, "E9.8.1.3", {"start": v(-23, 22.8) * mm, "end": v(-20, 24.54) * mm});
            skLineSegment(sketch, "E9.11.1.3", {"start": v(-20, 24.54) * mm, "end": v(-17, 22.8) * mm});
            skPoint(sketch, "E9.14.1.3", {"position": v(-18.5, 18.47) * mm});
            skPoint(sketch, "E9.15.1.3", {"position": v(-22.5, 25.4) * mm});
            skLineSegment(sketch, "E9.16.1.3", {"start": v(-17, 22.8) * mm, "end": v(-17, 19.34) * mm});
            skLineSegment(sketch, "E9.19.1.3", {"start": v(-21, 29.73) * mm, "end": v(-21, 26.27) * mm});
            skLineSegment(sketch, "E9.22.1.3", {"start": v(-24, 31.46) * mm, "end": v(-21, 29.73) * mm});
            skLineSegment(sketch, "E9.25.1.3", {"start": v(-27, 29.73) * mm, "end": v(-24, 31.46) * mm});
            skLineSegment(sketch, "E9.28.1.3", {"start": v(-27, 26.27) * mm, "end": v(-27, 29.73) * mm});
            skLineSegment(sketch, "E9.31.1.3", {"start": v(-24, 24.54) * mm, "end": v(-27, 26.27) * mm});
            skCircle(sketch, "E9.34.1.3", {"center": v(-24, 28) * mm, "radius": 3 * mm, "construction": true});
            skLineSegment(sketch, "E9.36.1.3", {"start": v(-17, 19.34) * mm, "end": v(-20, 17.6) * mm});
            skLineSegment(sketch, "E9.39.1.3", {"start": v(-21, 26.27) * mm, "end": v(-24, 24.54) * mm});
            skCircle(sketch, "E9.0.2.3", {"center": v(-12, 21.07) * mm, "radius": 3 * mm, "construction": true});
            skLineSegment(sketch, "E9.2.2.3", {"start": v(-12, 17.6) * mm, "end": v(-15, 19.34) * mm});
            skLineSegment(sketch, "E9.5.2.3", {"start": v(-15, 19.34) * mm, "end": v(-15, 22.8) * mm});
            skLineSegment(sketch, "E9.8.2.3", {"start": v(-15, 22.8) * mm, "end": v(-12, 24.54) * mm});
            skLineSegment(sketch, "E9.11.2.3", {"start": v(-12, 24.54) * mm, "end": v(-9, 22.8) * mm});
            skPoint(sketch, "E9.14.2.3", {"position": v(-10.5, 18.47) * mm});
            skPoint(sketch, "E9.15.2.3", {"position": v(-14.5, 25.4) * mm});
            skLineSegment(sketch, "E9.16.2.3", {"start": v(-9, 22.8) * mm, "end": v(-9, 19.34) * mm});
            skLineSegment(sketch, "E9.19.2.3", {"start": v(-13, 29.73) * mm, "end": v(-13, 26.27) * mm});
            skLineSegment(sketch, "E9.22.2.3", {"start": v(-16, 31.46) * mm, "end": v(-13, 29.73) * mm});
            skLineSegment(sketch, "E9.25.2.3", {"start": v(-19, 29.73) * mm, "end": v(-16, 31.46) * mm});
            skLineSegment(sketch, "E9.28.2.3", {"start": v(-19, 26.27) * mm, "end": v(-19, 29.73) * mm});
            skLineSegment(sketch, "E9.31.2.3", {"start": v(-16, 24.54) * mm, "end": v(-19, 26.27) * mm});
            skCircle(sketch, "E9.34.2.3", {"center": v(-16, 28) * mm, "radius": 3 * mm, "construction": true});
            skLineSegment(sketch, "E9.36.2.3", {"start": v(-9, 19.34) * mm, "end": v(-12, 17.6) * mm});
            skLineSegment(sketch, "E9.39.2.3", {"start": v(-13, 26.27) * mm, "end": v(-16, 24.54) * mm});
            skCircle(sketch, "E9.0.3.3", {"center": v(-4, 21.07) * mm, "radius": 3 * mm, "construction": true});
            skLineSegment(sketch, "E9.2.3.3", {"start": v(-4, 17.6) * mm, "end": v(-7, 19.34) * mm});
            skLineSegment(sketch, "E9.5.3.3", {"start": v(-7, 19.34) * mm, "end": v(-7, 22.8) * mm});
            skLineSegment(sketch, "E9.8.3.3", {"start": v(-7, 22.8) * mm, "end": v(-4, 24.54) * mm});
            skLineSegment(sketch, "E9.11.3.3", {"start": v(-4, 24.54) * mm, "end": v(-1, 22.8) * mm});
            skPoint(sketch, "E9.14.3.3", {"position": v(-2.5, 18.47) * mm});
            skPoint(sketch, "E9.15.3.3", {"position": v(-6.5, 25.4) * mm});
            skLineSegment(sketch, "E9.16.3.3", {"start": v(-1, 22.8) * mm, "end": v(-1, 19.34) * mm});
            skLineSegment(sketch, "E9.19.3.3", {"start": v(-5, 29.73) * mm, "end": v(-5, 26.27) * mm});
            skLineSegment(sketch, "E9.22.3.3", {"start": v(-8, 31.46) * mm, "end": v(-5, 29.73) * mm});
            skLineSegment(sketch, "E9.25.3.3", {"start": v(-11, 29.73) * mm, "end": v(-8, 31.46) * mm});
            skLineSegment(sketch, "E9.28.3.3", {"start": v(-11, 26.27) * mm, "end": v(-11, 29.73) * mm});
            skLineSegment(sketch, "E9.31.3.3", {"start": v(-8, 24.54) * mm, "end": v(-11, 26.27) * mm});
            skCircle(sketch, "E9.34.3.3", {"center": v(-8, 28) * mm, "radius": 3 * mm, "construction": true});
            skLineSegment(sketch, "E9.36.3.3", {"start": v(-1, 19.34) * mm, "end": v(-4, 17.6) * mm});
            skLineSegment(sketch, "E9.39.3.3", {"start": v(-5, 26.27) * mm, "end": v(-8, 24.54) * mm});
            skCircle(sketch, "E9.0.4.3", {"center": v(4, 21.07) * mm, "radius": 3 * mm, "construction": true});
            skLineSegment(sketch, "E9.2.4.3", {"start": v(4, 17.6) * mm, "end": v(1, 19.34) * mm});
            skLineSegment(sketch, "E9.5.4.3", {"start": v(1, 19.34) * mm, "end": v(1, 22.8) * mm});
            skLineSegment(sketch, "E9.8.4.3", {"start": v(1, 22.8) * mm, "end": v(4, 24.54) * mm});
            skLineSegment(sketch, "E9.11.4.3", {"start": v(4, 24.54) * mm, "end": v(7, 22.8) * mm});
            skPoint(sketch, "E9.14.4.3", {"position": v(5.5, 18.47) * mm});
            skPoint(sketch, "E9.15.4.3", {"position": v(1.5, 25.4) * mm});
            skLineSegment(sketch, "E9.16.4.3", {"start": v(7, 22.8) * mm, "end": v(7, 19.34) * mm});
            skLineSegment(sketch, "E9.19.4.3", {"start": v(3, 29.73) * mm, "end": v(3, 26.27) * mm});
            skLineSegment(sketch, "E9.22.4.3", {"start": v(0, 31.46) * mm, "end": v(3, 29.73) * mm});
            skLineSegment(sketch, "E9.25.4.3", {"start": v(-3, 29.73) * mm, "end": v(0, 31.46) * mm});
            skLineSegment(sketch, "E9.28.4.3", {"start": v(-3, 26.27) * mm, "end": v(-3, 29.73) * mm});
            skLineSegment(sketch, "E9.31.4.3", {"start": v(0, 24.54) * mm, "end": v(-3, 26.27) * mm});
            skCircle(sketch, "E9.34.4.3", {"center": v(0, 28) * mm, "radius": 3 * mm, "construction": true});
            skLineSegment(sketch, "E9.36.4.3", {"start": v(7, 19.34) * mm, "end": v(4, 17.6) * mm});
            skLineSegment(sketch, "E9.39.4.3", {"start": v(3, 26.27) * mm, "end": v(0, 24.54) * mm});
            skCircle(sketch, "E9.0.5.3", {"center": v(12, 21.07) * mm, "radius": 3 * mm, "construction": true});
            skLineSegment(sketch, "E9.2.5.3", {"start": v(12, 17.6) * mm, "end": v(9, 19.34) * mm});
            skLineSegment(sketch, "E9.5.5.3", {"start": v(9, 19.34) * mm, "end": v(9, 22.8) * mm});
            skLineSegment(sketch, "E9.8.5.3", {"start": v(9, 22.8) * mm, "end": v(12, 24.54) * mm});
            skLineSegment(sketch, "E9.11.5.3", {"start": v(12, 24.54) * mm, "end": v(15, 22.8) * mm});
            skPoint(sketch, "E9.14.5.3", {"position": v(13.5, 18.47) * mm});
            skPoint(sketch, "E9.15.5.3", {"position": v(9.5, 25.4) * mm});
            skLineSegment(sketch, "E9.16.5.3", {"start": v(15, 22.8) * mm, "end": v(15, 19.34) * mm});
            skLineSegment(sketch, "E9.19.5.3", {"start": v(11, 29.73) * mm, "end": v(11, 26.27) * mm});
            skLineSegment(sketch, "E9.22.5.3", {"start": v(8, 31.46) * mm, "end": v(11, 29.73) * mm});
            skLineSegment(sketch, "E9.25.5.3", {"start": v(5, 29.73) * mm, "end": v(8, 31.46) * mm});
            skLineSegment(sketch, "E9.28.5.3", {"start": v(5, 26.27) * mm, "end": v(5, 29.73) * mm});
            skLineSegment(sketch, "E9.31.5.3", {"start": v(8, 24.54) * mm, "end": v(5, 26.27) * mm});
            skCircle(sketch, "E9.34.5.3", {"center": v(8, 28) * mm, "radius": 3 * mm, "construction": true});
            skLineSegment(sketch, "E9.36.5.3", {"start": v(15, 19.34) * mm, "end": v(12, 17.6) * mm});
            skLineSegment(sketch, "E9.39.5.3", {"start": v(11, 26.27) * mm, "end": v(8, 24.54) * mm});
            skCircle(sketch, "E9.0.6.3", {"center": v(20, 21.07) * mm, "radius": 3 * mm, "construction": true});
            skLineSegment(sketch, "E9.2.6.3", {"start": v(20, 17.6) * mm, "end": v(17, 19.34) * mm});
            skLineSegment(sketch, "E9.5.6.3", {"start": v(17, 19.34) * mm, "end": v(17, 22.8) * mm});
            skLineSegment(sketch, "E9.8.6.3", {"start": v(17, 22.8) * mm, "end": v(20, 24.54) * mm});
            skLineSegment(sketch, "E9.11.6.3", {"start": v(20, 24.54) * mm, "end": v(23, 22.8) * mm});
            skPoint(sketch, "E9.14.6.3", {"position": v(21.5, 18.47) * mm});
            skPoint(sketch, "E9.15.6.3", {"position": v(17.5, 25.4) * mm});
            skLineSegment(sketch, "E9.16.6.3", {"start": v(23, 22.8) * mm, "end": v(23, 19.34) * mm});
            skLineSegment(sketch, "E9.19.6.3", {"start": v(19, 29.73) * mm, "end": v(19, 26.27) * mm});
            skLineSegment(sketch, "E9.22.6.3", {"start": v(16, 31.46) * mm, "end": v(19, 29.73) * mm});
            skLineSegment(sketch, "E9.25.6.3", {"start": v(13, 29.73) * mm, "end": v(16, 31.46) * mm});
            skLineSegment(sketch, "E9.28.6.3", {"start": v(13, 26.27) * mm, "end": v(13, 29.73) * mm});
            skLineSegment(sketch, "E9.31.6.3", {"start": v(16, 24.54) * mm, "end": v(13, 26.27) * mm});
            skCircle(sketch, "E9.34.6.3", {"center": v(16, 28) * mm, "radius": 3 * mm, "construction": true});
            skLineSegment(sketch, "E9.36.6.3", {"start": v(23, 19.34) * mm, "end": v(20, 17.6) * mm});
            skLineSegment(sketch, "E9.39.6.3", {"start": v(19, 26.27) * mm, "end": v(16, 24.54) * mm});
            skCircle(sketch, "E9.0.7.3", {"center": v(28, 21.07) * mm, "radius": 3 * mm, "construction": true});
            skLineSegment(sketch, "E9.2.7.3", {"start": v(28, 17.6) * mm, "end": v(25, 19.34) * mm});
            skLineSegment(sketch, "E9.5.7.3", {"start": v(25, 19.34) * mm, "end": v(25, 22.8) * mm});
            skLineSegment(sketch, "E9.8.7.3", {"start": v(25, 22.8) * mm, "end": v(28, 24.54) * mm});
            skLineSegment(sketch, "E9.11.7.3", {"start": v(28, 24.54) * mm, "end": v(31, 22.8) * mm});
            skPoint(sketch, "E9.14.7.3", {"position": v(29.5, 18.47) * mm});
            skPoint(sketch, "E9.15.7.3", {"position": v(25.5, 25.4) * mm});
            skLineSegment(sketch, "E9.16.7.3", {"start": v(31, 22.8) * mm, "end": v(31, 19.34) * mm});
            skLineSegment(sketch, "E9.19.7.3", {"start": v(27, 29.73) * mm, "end": v(27, 26.27) * mm});
            skLineSegment(sketch, "E9.22.7.3", {"start": v(24, 31.46) * mm, "end": v(27, 29.73) * mm});
            skLineSegment(sketch, "E9.25.7.3", {"start": v(21, 29.73) * mm, "end": v(24, 31.46) * mm});
            skLineSegment(sketch, "E9.28.7.3", {"start": v(21, 26.27) * mm, "end": v(21, 29.73) * mm});
            skLineSegment(sketch, "E9.31.7.3", {"start": v(24, 24.54) * mm, "end": v(21, 26.27) * mm});
            skCircle(sketch, "E9.34.7.3", {"center": v(24, 28) * mm, "radius": 3 * mm, "construction": true});
            skLineSegment(sketch, "E9.36.7.3", {"start": v(31, 19.34) * mm, "end": v(28, 17.6) * mm});
            skLineSegment(sketch, "E9.39.7.3", {"start": v(27, 26.27) * mm, "end": v(24, 24.54) * mm});
            skCircle(sketch, "E9.0.8.3", {"center": v(36, 21.07) * mm, "radius": 3 * mm, "construction": true});
            skLineSegment(sketch, "E9.2.8.3", {"start": v(36, 17.6) * mm, "end": v(33, 19.34) * mm});
            skLineSegment(sketch, "E9.5.8.3", {"start": v(33, 19.34) * mm, "end": v(33, 22.8) * mm});
            skLineSegment(sketch, "E9.8.8.3", {"start": v(33, 22.8) * mm, "end": v(36, 24.54) * mm});
            skLineSegment(sketch, "E9.11.8.3", {"start": v(36, 24.54) * mm, "end": v(39, 22.8) * mm});
            skPoint(sketch, "E9.14.8.3", {"position": v(37.5, 18.47) * mm});
            skPoint(sketch, "E9.15.8.3", {"position": v(33.5, 25.4) * mm});
            skLineSegment(sketch, "E9.16.8.3", {"start": v(39, 22.8) * mm, "end": v(39, 19.34) * mm});
            skLineSegment(sketch, "E9.19.8.3", {"start": v(35, 29.73) * mm, "end": v(35, 26.27) * mm});
            skLineSegment(sketch, "E9.22.8.3", {"start": v(32, 31.46) * mm, "end": v(35, 29.73) * mm});
            skLineSegment(sketch, "E9.25.8.3", {"start": v(29, 29.73) * mm, "end": v(32, 31.46) * mm});
            skLineSegment(sketch, "E9.28.8.3", {"start": v(29, 26.27) * mm, "end": v(29, 29.73) * mm});
            skLineSegment(sketch, "E9.31.8.3", {"start": v(32, 24.54) * mm, "end": v(29, 26.27) * mm});
            skCircle(sketch, "E9.34.8.3", {"center": v(32, 28) * mm, "radius": 3 * mm, "construction": true});
            skLineSegment(sketch, "E9.36.8.3", {"start": v(39, 19.34) * mm, "end": v(36, 17.6) * mm});
            skLineSegment(sketch, "E9.39.8.3", {"start": v(35, 26.27) * mm, "end": v(32, 24.54) * mm});
            skCircle(sketch, "E9.0.9.3", {"center": v(44, 21.07) * mm, "radius": 3 * mm, "construction": true});
            skLineSegment(sketch, "E9.2.9.3", {"start": v(44, 17.6) * mm, "end": v(41, 19.34) * mm});
            skLineSegment(sketch, "E9.5.9.3", {"start": v(41, 19.34) * mm, "end": v(41, 22.8) * mm});
            skLineSegment(sketch, "E9.8.9.3", {"start": v(41, 22.8) * mm, "end": v(44, 24.54) * mm});
            skLineSegment(sketch, "E9.11.9.3", {"start": v(44, 24.54) * mm, "end": v(47, 22.8) * mm});
            skPoint(sketch, "E9.14.9.3", {"position": v(45.5, 18.47) * mm});
            skPoint(sketch, "E9.15.9.3", {"position": v(41.5, 25.4) * mm});
            skLineSegment(sketch, "E9.16.9.3", {"start": v(47, 22.8) * mm, "end": v(47, 19.34) * mm});
            skLineSegment(sketch, "E9.19.9.3", {"start": v(43, 29.73) * mm, "end": v(43, 26.27) * mm});
            skLineSegment(sketch, "E9.22.9.3", {"start": v(40, 31.46) * mm, "end": v(43, 29.73) * mm});
            skLineSegment(sketch, "E9.25.9.3", {"start": v(37, 29.73) * mm, "end": v(40, 31.46) * mm});
            skLineSegment(sketch, "E9.28.9.3", {"start": v(37, 26.27) * mm, "end": v(37, 29.73) * mm});
            skLineSegment(sketch, "E9.31.9.3", {"start": v(40, 24.54) * mm, "end": v(37, 26.27) * mm});
            skCircle(sketch, "E9.34.9.3", {"center": v(40, 28) * mm, "radius": 3 * mm, "construction": true});
            skLineSegment(sketch, "E9.36.9.3", {"start": v(47, 19.34) * mm, "end": v(44, 17.6) * mm});
            skLineSegment(sketch, "E9.39.9.3", {"start": v(43, 26.27) * mm, "end": v(40, 24.54) * mm});
            skCircle(sketch, "E9.0.10.3", {"center": v(52, 21.07) * mm, "radius": 3 * mm, "construction": true});
            skLineSegment(sketch, "E9.2.10.3", {"start": v(52, 17.6) * mm, "end": v(49, 19.34) * mm});
            skLineSegment(sketch, "E9.5.10.3", {"start": v(49, 19.34) * mm, "end": v(49, 22.8) * mm});
            skLineSegment(sketch, "E9.8.10.3", {"start": v(49, 22.8) * mm, "end": v(52, 24.54) * mm});
            skLineSegment(sketch, "E9.11.10.3", {"start": v(52, 24.54) * mm, "end": v(55, 22.8) * mm});
            skPoint(sketch, "E9.14.10.3", {"position": v(53.5, 18.47) * mm});
            skPoint(sketch, "E9.15.10.3", {"position": v(49.5, 25.4) * mm});
            skLineSegment(sketch, "E9.16.10.3", {"start": v(55, 22.8) * mm, "end": v(55, 19.34) * mm});
            skLineSegment(sketch, "E9.19.10.3", {"start": v(51, 29.73) * mm, "end": v(51, 26.27) * mm});
            skLineSegment(sketch, "E9.22.10.3", {"start": v(48, 31.46) * mm, "end": v(51, 29.73) * mm});
            skLineSegment(sketch, "E9.25.10.3", {"start": v(45, 29.73) * mm, "end": v(48, 31.46) * mm});
            skLineSegment(sketch, "E9.28.10.3", {"start": v(45, 26.27) * mm, "end": v(45, 29.73) * mm});
            skLineSegment(sketch, "E9.31.10.3", {"start": v(48, 24.54) * mm, "end": v(45, 26.27) * mm});
            skCircle(sketch, "E9.34.10.3", {"center": v(48, 28) * mm, "radius": 3 * mm, "construction": true});
            skLineSegment(sketch, "E9.36.10.3", {"start": v(55, 19.34) * mm, "end": v(52, 17.6) * mm});
            skLineSegment(sketch, "E9.39.10.3", {"start": v(51, 26.27) * mm, "end": v(48, 24.54) * mm});
            skCircle(sketch, "E9.0.11.3", {"center": v(60, 21.07) * mm, "radius": 3 * mm, "construction": true});
            skLineSegment(sketch, "E9.2.11.3", {"start": v(60, 17.6) * mm, "end": v(57, 19.34) * mm});
            skLineSegment(sketch, "E9.5.11.3", {"start": v(57, 19.34) * mm, "end": v(57, 22.8) * mm});
            skLineSegment(sketch, "E9.8.11.3", {"start": v(57, 22.8) * mm, "end": v(60, 24.54) * mm});
            skLineSegment(sketch, "E9.11.11.3", {"start": v(60, 24.54) * mm, "end": v(63, 22.8) * mm});
            skPoint(sketch, "E9.14.11.3", {"position": v(61.5, 18.47) * mm});
            skPoint(sketch, "E9.15.11.3", {"position": v(57.5, 25.4) * mm});
            skLineSegment(sketch, "E9.16.11.3", {"start": v(63, 22.8) * mm, "end": v(63, 19.34) * mm});
            skLineSegment(sketch, "E9.19.11.3", {"start": v(59, 29.73) * mm, "end": v(59, 26.27) * mm});
            skLineSegment(sketch, "E9.22.11.3", {"start": v(56, 31.46) * mm, "end": v(59, 29.73) * mm});
            skLineSegment(sketch, "E9.25.11.3", {"start": v(53, 29.73) * mm, "end": v(56, 31.46) * mm});
            skLineSegment(sketch, "E9.28.11.3", {"start": v(53, 26.27) * mm, "end": v(53, 29.73) * mm});
            skLineSegment(sketch, "E9.31.11.3", {"start": v(56, 24.54) * mm, "end": v(53, 26.27) * mm});
            skCircle(sketch, "E9.34.11.3", {"center": v(56, 28) * mm, "radius": 3 * mm, "construction": true});
            skLineSegment(sketch, "E9.36.11.3", {"start": v(63, 19.34) * mm, "end": v(60, 17.6) * mm});
            skLineSegment(sketch, "E9.39.11.3", {"start": v(59, 26.27) * mm, "end": v(56, 24.54) * mm});
            skCircle(sketch, "E9.0.12.3", {"center": v(68, 21.07) * mm, "radius": 3 * mm, "construction": true});
            skLineSegment(sketch, "E9.2.12.3", {"start": v(68, 17.6) * mm, "end": v(65, 19.34) * mm});
            skLineSegment(sketch, "E9.5.12.3", {"start": v(65, 19.34) * mm, "end": v(65, 22.8) * mm});
            skLineSegment(sketch, "E9.8.12.3", {"start": v(65, 22.8) * mm, "end": v(68, 24.54) * mm});
            skLineSegment(sketch, "E9.11.12.3", {"start": v(68, 24.54) * mm, "end": v(71, 22.8) * mm});
            skPoint(sketch, "E9.14.12.3", {"position": v(69.5, 18.47) * mm});
            skPoint(sketch, "E9.15.12.3", {"position": v(65.5, 25.4) * mm});
            skLineSegment(sketch, "E9.16.12.3", {"start": v(71, 22.8) * mm, "end": v(71, 19.34) * mm});
            skLineSegment(sketch, "E9.19.12.3", {"start": v(67, 29.73) * mm, "end": v(67, 26.27) * mm});
            skLineSegment(sketch, "E9.22.12.3", {"start": v(64, 31.46) * mm, "end": v(67, 29.73) * mm});
            skLineSegment(sketch, "E9.25.12.3", {"start": v(61, 29.73) * mm, "end": v(64, 31.46) * mm});
            skLineSegment(sketch, "E9.28.12.3", {"start": v(61, 26.27) * mm, "end": v(61, 29.73) * mm});
            skLineSegment(sketch, "E9.31.12.3", {"start": v(64, 24.54) * mm, "end": v(61, 26.27) * mm});
            skCircle(sketch, "E9.34.12.3", {"center": v(64, 28) * mm, "radius": 3 * mm, "construction": true});
            skLineSegment(sketch, "E9.36.12.3", {"start": v(71, 19.34) * mm, "end": v(68, 17.6) * mm});
            skLineSegment(sketch, "E9.39.12.3", {"start": v(67, 26.27) * mm, "end": v(64, 24.54) * mm});
            skSolve(sketch);
        }
        {
            var Q0;
            Q0=makeQuery(id+"F0.imprint","IMPRINT",FACE,{"disambiguationData":[TD([[makeQuery(id+"F0.imprint","IMPRINT",EDGE,{"derivedFrom":sQuery(id+"F0.wireOp",EDGE,"E0.0")}),1.0]])]});
            extrude(context, id + "F1", {"entities" : qUnion([Q0]), "oppositeDirection" : true, "depth" : 1.5 * mm});
        }
        {
            var Q0;
            Q0=makeQuery(id+"F0.imprint","IMPRINT",FACE,{"disambiguationData":[TD([[makeQuery(id+"F0.imprint","IMPRINT",EDGE,{"derivedFrom":sQuery(id+"F0.wireOp",EDGE,"E3.bottom")}),1.0]])]});
            extrude(context, id + "F2", {"entities" : qUnion([Q0]), "operationType" : NewBodyOperationType.ADD, "oppositeDirection" : true, "depth" : 28 * mm});
        }
        {
            var Q0;
            Q0=makeQuery(id+"F2.opExtrude","CAP_FACE",FACE,{"disambiguationData":[OSD([sQuery(id+"F0.wireOp",EDGE,"E3.bottom"),sQuery(id+"F0.wireOp",EDGE,"E3.top"),sQuery(id+"F0.wireOp",EDGE,"E3.left"),sQuery(id+"F0.wireOp",EDGE,"E3.right"),sQuery(id+"F0.wireOp",EDGE,"E6.bottom"),sQuery(id+"F0.wireOp",EDGE,"E6.top"),sQuery(id+"F0.wireOp",EDGE,"E6.left"),sQuery(id+"F0.wireOp",EDGE,"E6.right")])],"isStart":false});
            var sketch = newSketch(context, id + "F3", { "sketchPlane" : qUnion([Q0])});
            skCircle(sketch, "E10", {"center": v(-33, -18.1) * mm, "radius": 1.5 * mm});
            skCircle(sketch, "E11", {"center": v(-33, -18.1) * mm, "radius": 4 * mm});
            skLineSegment(sketch, "E12", {"start": v(-33, -14.1) * mm, "end": v(-38, -14.1) * mm});
            skLineSegment(sketch, "E13", {"start": v(-33, -22.1) * mm, "end": v(-38, -22.1) * mm});
            skCircle(sketch, "E14", {"center": v(69, -18.1) * mm, "radius": 1.5 * mm});
            skCircle(sketch, "E15", {"center": v(69, -18.1) * mm, "radius": 4 * mm});
            skLineSegment(sketch, "E16", {"start": v(69, -14.1) * mm, "end": v(74, -14.1) * mm});
            skLineSegment(sketch, "E17", {"start": v(69, -22.1) * mm, "end": v(74, -22.1) * mm});
            skSolve(sketch);
        }
        {
            var Q0;
            Q0=makeQuery(id+"F3.imprint","IMPRINT",FACE,{"disambiguationData":[TD([[makeQuery(id+"F3.imprint","IMPRINT",EDGE,{"derivedFrom":sQuery(id+"F3.wireOp",EDGE,"RaHO4GLc-gHrY-JM8G-Uk0o-D8coDqmXbqgz")}),-1.0]])]});
            var Q1;
            Q1=makeQuery(id+"F3.imprint","IMPRINT",FACE,{"disambiguationData":[TD([[makeQuery(id+"F3.imprint","IMPRINT",EDGE,{"derivedFrom":sQuery(id+"F3.wireOp",EDGE,"P8YlM1Qx-9nVZ-rCij-MPQd-DoSFTgI6x59o")}),-1.0]])]});
            var Q2;
            {var subQ0=sQuery(id+"F3.wireOp",EDGE,"E16");Q2=makeQuery(id+"F3.imprint","IMPRINT",FACE,{"disambiguationData":[TD([[makeQuery(id+"F3.imprint","IMPRINT",EDGE,{"derivedFrom":subQ0}),-1.0]])]});}
            var Q3;
            Q3=makeQuery(id+"F3.imprint","IMPRINT",FACE,{"disambiguationData":[TD([[makeQuery(id+"F3.imprint","IMPRINT",EDGE,{"derivedFrom":sQuery(id+"F3.wireOp",EDGE,"E14")}),-1.0]])]});
            var Q4;
            {var subQ0=sQuery(id+"F3.wireOp",EDGE,"E12");Q4=makeQuery(id+"F3.imprint","IMPRINT",FACE,{"disambiguationData":[TD([[makeQuery(id+"F3.imprint","IMPRINT",EDGE,{"derivedFrom":subQ0}),1.0]])]});}
            var Q5;
            Q5=makeQuery(id+"F3.imprint","IMPRINT",FACE,{"disambiguationData":[TD([[makeQuery(id+"F3.imprint","IMPRINT",EDGE,{"derivedFrom":sQuery(id+"F3.wireOp",EDGE,"E10")}),-1.0]])]});
            extrude(context, id + "F4", {"entities" : qUnion([Q0, Q1, Q2, Q3, Q4, Q5]), "operationType" : NewBodyOperationType.ADD, "oppositeDirection" : true, "depth" : 2 * mm});
        }
        {
            var Q0;
            Q0=makeQuery(id+"F2.opExtrude","SWEPT_FACE",FACE,{"disambiguationData":[OSD([sQuery(id+"F0.wireOp",EDGE,"E6.bottom")])]});
            var sketch = newSketch(context, id + "F5", { "sketchPlane" : qUnion([Q0])});
            skLineSegment(sketch, "E18.bottom", {"start": v(-75.5, -28) * mm, "end": v(-50.5, -28) * mm});
            skLineSegment(sketch, "E18.top", {"start": v(-75.5, -20) * mm, "end": v(-50.5, -20) * mm});
            skLineSegment(sketch, "E18.left", {"start": v(-75.5, -28) * mm, "end": v(-75.5, -20) * mm});
            skLineSegment(sketch, "E18.right", {"start": v(-50.5, -28) * mm, "end": v(-50.5, -20) * mm});
            skLineSegment(sketch, "E19", {"start": v(-18, 19.7) * mm, "end": v(-18, -41) * mm, "construction": true});
            skLineSegment(sketch, "E20.MirrorCS", {"start": v(39.5, -20) * mm, "end": v(14.5, -20) * mm});
            skLineSegment(sketch, "E21.MirrorCS", {"start": v(14.5, -28) * mm, "end": v(14.5, -20) * mm});
            skSolve(sketch);
        }
        {
            var Q0;
            Q0=makeQuery(id+"F2.opExtrude","SWEPT_FACE",FACE,{"disambiguationData":[OSD([sQuery(id+"F0.wireOp",EDGE,"E6.right")])]});
            var sketch = newSketch(context, id + "F6", { "sketchPlane" : qUnion([Q0])});
            skLineSegment(sketch, "E22.bottom", {"start": v(37.1, -28) * mm, "end": v(23.1, -28) * mm});
            skLineSegment(sketch, "E22.top", {"start": v(37.1, -20) * mm, "end": v(23.1, -20) * mm});
            skLineSegment(sketch, "E22.left", {"start": v(37.1, -28) * mm, "end": v(37.1, -20) * mm});
            skLineSegment(sketch, "E22.right", {"start": v(23.1, -28) * mm, "end": v(23.1, -20) * mm});
            skLineSegment(sketch, "E23.bottom", {"start": v(-29.9, -28) * mm, "end": v(10.1, -28) * mm});
            skLineSegment(sketch, "E23.top", {"start": v(-29.9, -10) * mm, "end": v(10.1, -10) * mm});
            skLineSegment(sketch, "E23.left", {"start": v(-29.9, -28) * mm, "end": v(-29.9, -10) * mm});
            skLineSegment(sketch, "E23.right", {"start": v(10.1, -28) * mm, "end": v(10.1, -10) * mm});
            skSolve(sketch);
        }
        {
            var Q0;
            Q0=makeQuery(id+"F2.opExtrude","SWEPT_FACE",FACE,{"disambiguationData":[OSD([sQuery(id+"F0.wireOp",EDGE,"E6.left")])]});
            var sketch = newSketch(context, id + "F7", { "sketchPlane" : qUnion([Q0])});
            skLineSegment(sketch, "E24.bottom", {"start": v(-10.1, -28) * mm, "end": v(29.9, -28) * mm});
            skLineSegment(sketch, "E24.top", {"start": v(-10.1, -20) * mm, "end": v(29.9, -20) * mm});
            skLineSegment(sketch, "E24.left", {"start": v(-10.1, -28) * mm, "end": v(-10.1, -20) * mm});
            skLineSegment(sketch, "E24.right", {"start": v(29.9, -28) * mm, "end": v(29.9, -20) * mm});
            skSolve(sketch);
        }
        {
            var Q0;
            Q0=makeQuery(id+"F2.opExtrude","SWEPT_FACE",FACE,{"disambiguationData":[OSD([sQuery(id+"F0.wireOp",EDGE,"E6.top")])]});
            var sketch = newSketch(context, id + "F8", { "sketchPlane" : qUnion([Q0])});
            skLineSegment(sketch, "E25.bottom", {"start": v(-35.5, -28) * mm, "end": v(71.5, -28) * mm});
            skLineSegment(sketch, "E25.top", {"start": v(-35.5, -5) * mm, "end": v(71.5, -5) * mm});
            skLineSegment(sketch, "E25.left", {"start": v(-35.5, -28) * mm, "end": v(-35.5, -5) * mm});
            skLineSegment(sketch, "E25.right", {"start": v(71.5, -28) * mm, "end": v(71.5, -5) * mm});
            skSolve(sketch);
        }
        {
            var Q0;
            Q0=makeQuery(id+"F5.imprint","IMPRINT",FACE,{"disambiguationData":[TD([[makeQuery(id+"F5.imprint","IMPRINT",EDGE,{"derivedFrom":sQuery(id+"F5.wireOp",EDGE,"E18.bottom")}),-1.0]])]});
            var Q1;
            {var subQ0=sQuery(id+"F5.wireOp",EDGE,"E20.MirrorCS");Q1=makeQuery(id+"F5.imprint","IMPRINT",FACE,{"disambiguationData":[TD([[makeQuery(id+"F5.imprint","IMPRINT",EDGE,{"derivedFrom":subQ0}),1.0]])]});}
            extrude(context, id + "F9", {"entities" : qUnion([Q0, Q1]), "operationType" : NewBodyOperationType.REMOVE, "oppositeDirection" : true, "depth" : 14 * mm});
        }
        {
            var Q0;
            Q0=makeQuery(id+"F6.imprint","IMPRINT",FACE,{"disambiguationData":[TD([[makeQuery(id+"F6.imprint","IMPRINT",EDGE,{"derivedFrom":sQuery(id+"F6.wireOp",EDGE,"E23.bottom")}),-1.0]])]});
            extrude(context, id + "F10", {"entities" : qUnion([Q0]), "operationType" : NewBodyOperationType.REMOVE, "oppositeDirection" : true, "depth" : 5 * mm});
        }
        {
            var Q0;
            Q0=makeQuery(id+"F7.imprint","IMPRINT",FACE,{"disambiguationData":[TD([[makeQuery(id+"F7.imprint","IMPRINT",EDGE,{"derivedFrom":sQuery(id+"F7.wireOp",EDGE,"E24.bottom")}),1.0]])]});
            extrude(context, id + "F11", {"entities" : qUnion([Q0]), "operationType" : NewBodyOperationType.REMOVE, "oppositeDirection" : true, "depth" : 5 * mm});
        }
        {
            var Q0;
            Q0=makeQuery(id+"F8.imprint","IMPRINT",FACE,{"disambiguationData":[TD([[makeQuery(id+"F8.imprint","IMPRINT",EDGE,{"derivedFrom":sQuery(id+"F8.wireOp",EDGE,"E25.bottom")}),1.0]])]});
            extrude(context, id + "F12", {"entities" : qUnion([Q0]), "operationType" : NewBodyOperationType.REMOVE, "oppositeDirection" : true, "depth" : 2 * mm});
        }
        {
            var Q0;
            Q0=makeQuery(id+"F1.opExtrude","CAP_EDGE",EDGE,{"disambiguationData":[OSD([sQuery(id+"F0.wireOp",EDGE,"E3.bottom")])],"isStart":false});
            var Q1;
            Q1=makeQuery(id+"F2.opExtrude","SWEPT_EDGE",EDGE,{"disambiguationData":[OSD([sQuery(id+"F0.wireOp",EDGE,"E3.bottom"),sQuery(id+"F0.wireOp",EDGE,"E3.right")])]});
            var Q2;
            Q2=makeQuery(id+"F1.opExtrude","CAP_EDGE",EDGE,{"disambiguationData":[OSD([sQuery(id+"F0.wireOp",EDGE,"E3.right")])],"isStart":false});
            var Q3;
            Q3=makeQuery(id+"F1.opExtrude","CAP_EDGE",EDGE,{"disambiguationData":[OSD([sQuery(id+"F0.wireOp",EDGE,"E3.left")])],"isStart":false});
            var Q4;
            Q4=makeQuery(id+"F2.opExtrude","SWEPT_EDGE",EDGE,{"disambiguationData":[OSD([sQuery(id+"F0.wireOp",EDGE,"E3.bottom"),sQuery(id+"F0.wireOp",EDGE,"E3.left")])]});
            var Q5;
            Q5=makeQuery(id+"F1.opExtrude","CAP_EDGE",EDGE,{"disambiguationData":[OSD([sQuery(id+"F0.wireOp",EDGE,"E3.top")])],"isStart":false});
            var Q6;
            Q6=makeQuery(id+"F4.opExtrude","SWEPT_EDGE",EDGE,{"disambiguationData":[OSD([sQuery(id+"F0.wireOp",EDGE,"E3.right"),sQuery(id+"F3.wireOp",EDGE,"E16")])]});
            var Q7;
            Q7=makeQuery(id+"F4.opExtrude","SWEPT_EDGE",EDGE,{"disambiguationData":[OSD([sQuery(id+"F0.wireOp",EDGE,"E3.right"),sQuery(id+"F3.wireOp",EDGE,"E17")])]});
            var Q8;
            Q8=makeQuery(id+"F4.opExtrude","SWEPT_EDGE",EDGE,{"disambiguationData":[OSD([sQuery(id+"F0.wireOp",EDGE,"E3.left"),sQuery(id+"F3.wireOp",EDGE,"E13")])]});
            var Q9;
            Q9=makeQuery(id+"F4.opExtrude","SWEPT_EDGE",EDGE,{"disambiguationData":[OSD([sQuery(id+"F0.wireOp",EDGE,"E3.left"),sQuery(id+"F3.wireOp",EDGE,"E12")])]});
            var Q10;
            Q10=makeQuery(id+"F11.boolean.opBoolean","COPY",EDGE,{"derivedFrom":makeQuery(id+"F11.opExtrude","SWEPT_EDGE",EDGE,{"disambiguationData":[OSD([sQuery(id+"F7.wireOp",EDGE,"E24.top"),sQuery(id+"F7.wireOp",EDGE,"E24.left")])]})});
            var Q11;
            Q11=makeQuery(id+"F9.boolean.opBoolean","COPY",EDGE,{"derivedFrom":makeQuery(id+"F9.opExtrude","CAP_EDGE",EDGE,{"disambiguationData":[OSD([sQuery(id+"F5.wireOp",EDGE,"E20.MirrorCS")])],"isStart":false})});
            var Q12;
            Q12=makeQuery(id+"F2.opExtrude","SWEPT_EDGE",EDGE,{"disambiguationData":[OSD([sQuery(id+"F0.wireOp",EDGE,"E3.top"),sQuery(id+"F0.wireOp",EDGE,"E3.left")])]});
            var Q13;
            Q13=makeQuery(id+"F2.opExtrude","SWEPT_EDGE",EDGE,{"disambiguationData":[OSD([sQuery(id+"F0.wireOp",EDGE,"E3.top"),sQuery(id+"F0.wireOp",EDGE,"E3.right")])]});
            var Q14;
            Q14=makeQuery(id+"F9.boolean.opBoolean","COPY",EDGE,{"derivedFrom":makeQuery(id+"F9.opExtrude","CAP_EDGE",EDGE,{"disambiguationData":[OSD([sQuery(id+"F5.wireOp",EDGE,"E18.top")])],"isStart":false})});
            var Q15;
            Q15=makeQuery(id+"F10.boolean.opBoolean","COPY",EDGE,{"derivedFrom":makeQuery(id+"F10.opExtrude","SWEPT_EDGE",EDGE,{"disambiguationData":[OSD([sQuery(id+"F6.wireOp",EDGE,"E23.top"),sQuery(id+"F6.wireOp",EDGE,"E23.right")])]})});
            var Q16;
            Q16=makeQuery(id+"F2.opExtrude","SWEPT_EDGE",EDGE,{"disambiguationData":[OSD([sQuery(id+"F0.wireOp",EDGE,"E6.top"),sQuery(id+"F0.wireOp",EDGE,"E6.right")])]});
            var Q17;
            Q17=makeQuery(id+"F2.opExtrude","SWEPT_EDGE",EDGE,{"disambiguationData":[OSD([sQuery(id+"F0.wireOp",EDGE,"E6.top"),sQuery(id+"F0.wireOp",EDGE,"E6.left")])]});
            var Q18;
            Q18=makeQuery(id+"F2.opExtrude","CAP_EDGE",EDGE,{"disambiguationData":[OSD([sQuery(id+"F0.wireOp",EDGE,"E6.left")])],"isStart":true});
            var Q19;
            Q19=makeQuery(id+"F2.opExtrude","CAP_EDGE",EDGE,{"disambiguationData":[OSD([sQuery(id+"F0.wireOp",EDGE,"E6.bottom")])],"isStart":true});
            var Q20;
            Q20=makeQuery(id+"F2.opExtrude","CAP_EDGE",EDGE,{"disambiguationData":[OSD([sQuery(id+"F0.wireOp",EDGE,"E6.right")])],"isStart":true});
            var Q21;
            Q21=makeQuery(id+"F2.opExtrude","CAP_EDGE",EDGE,{"disambiguationData":[OSD([sQuery(id+"F0.wireOp",EDGE,"E6.top")])],"isStart":true});
            var Q22;
            Q22=makeQuery(id+"F9.boolean.opBoolean","COPY",EDGE,{"derivedFrom":makeQuery(id+"F9.opExtrude","SWEPT_EDGE",EDGE,{"disambiguationData":[OSD([sQuery(id+"F5.wireOp",EDGE,"E18.top"),sQuery(id+"F5.wireOp",EDGE,"E18.right")])]})});
            var Q23;
            Q23=makeQuery(id+"F9.boolean.opBoolean","COPY",EDGE,{"derivedFrom":makeQuery(id+"F9.opExtrude","SWEPT_EDGE",EDGE,{"disambiguationData":[OSD([sQuery(id+"F0.wireOp",EDGE,"E6.bottom"),sQuery(id+"F5.wireOp",EDGE,"E18.bottom"),sQuery(id+"F5.wireOp",EDGE,"E18.right")])]})});
            var Q24;
            Q24=makeQuery(id+"F9.boolean.opBoolean","COPY",EDGE,{"derivedFrom":makeQuery(id+"F9.opExtrude","SWEPT_EDGE",EDGE,{"disambiguationData":[OSD([sQuery(id+"F0.wireOp",EDGE,"E6.bottom"),sQuery(id+"F5.wireOp",EDGE,"E21.MirrorCS")])]})});
            var Q25;
            Q25=makeQuery(id+"F9.boolean.opBoolean","COPY",EDGE,{"derivedFrom":makeQuery(id+"F9.opExtrude","SWEPT_EDGE",EDGE,{"disambiguationData":[OSD([sQuery(id+"F5.wireOp",EDGE,"E20.MirrorCS"),sQuery(id+"F5.wireOp",EDGE,"E21.MirrorCS")])]})});
            var Q26;
            Q26=makeQuery(id+"F2.opExtrude","SWEPT_EDGE",EDGE,{"disambiguationData":[OSD([sQuery(id+"F0.wireOp",EDGE,"E6.bottom"),sQuery(id+"F0.wireOp",EDGE,"E6.right")])]});
            var Q27;
            Q27=makeQuery(id+"F2.opExtrude","SWEPT_EDGE",EDGE,{"disambiguationData":[OSD([sQuery(id+"F0.wireOp",EDGE,"E6.bottom"),sQuery(id+"F0.wireOp",EDGE,"E6.left")])]});
            fillet(context, id + "F13", {"entities" : qUnion([Q0, Q1, Q2, Q3, Q4, Q5, Q6, Q7, Q8, Q9, Q10, Q11, Q12, Q13, Q14, Q15, Q16, Q17, Q18, Q19, Q20, Q21, Q22, Q23, Q24, Q25, Q26, Q27]), "radius" : 3 * mm, "tangentPropagation" : true, "allowEdgeOverflow" : false});
        }
        {
            var Q0;
            Q0=makeQuery(id+"F9.boolean.opBoolean","COPY",EDGE,{"derivedFrom":makeQuery(id+"F9.opExtrude","CAP_EDGE",EDGE,{"disambiguationData":[OSD([sQuery(id+"F5.wireOp",EDGE,"E18.bottom")])],"isStart":false})});
            var Q1;
            Q1=makeQuery(id+"F11.boolean.opBoolean","COPY",EDGE,{"derivedFrom":makeQuery(id+"F11.opExtrude","SWEPT_EDGE",EDGE,{"disambiguationData":[OSD([sQuery(id+"F0.wireOp",EDGE,"E6.left"),sQuery(id+"F7.wireOp",EDGE,"E24.bottom"),sQuery(id+"F7.wireOp",EDGE,"E24.left")])]})});
            var Q2;
            Q2=makeQuery(id+"F10.boolean.opBoolean","COPY",EDGE,{"derivedFrom":makeQuery(id+"F10.opExtrude","SWEPT_EDGE",EDGE,{"disambiguationData":[OSD([sQuery(id+"F0.wireOp",EDGE,"E6.right"),sQuery(id+"F6.wireOp",EDGE,"E23.bottom"),sQuery(id+"F6.wireOp",EDGE,"E23.right")])]})});
            var Q3;
            Q3=makeQuery(id+"F12.boolean.opBoolean","INTERSECT",EDGE,{"derivedFrom":[makeQuery(id+"F10.boolean.opBoolean","COPY",FACE,{"derivedFrom":makeQuery(id+"F10.opExtrude","SWEPT_FACE",FACE,{"disambiguationData":[OSD([sQuery(id+"F6.wireOp",EDGE,"E23.top")])]})}),makeQuery(id+"F12.opExtrude","SWEPT_FACE",FACE,{"disambiguationData":[OSD([sQuery(id+"F8.wireOp",EDGE,"E25.right")])]})]});
            var Q4;
            Q4=makeQuery(id+"F12.boolean.opBoolean","INTERSECT",EDGE,{"derivedFrom":[makeQuery(id+"F11.boolean.opBoolean","COPY",FACE,{"derivedFrom":makeQuery(id+"F11.opExtrude","SWEPT_FACE",FACE,{"disambiguationData":[OSD([sQuery(id+"F7.wireOp",EDGE,"E24.top")])]})}),makeQuery(id+"F12.opExtrude","SWEPT_FACE",FACE,{"disambiguationData":[OSD([sQuery(id+"F8.wireOp",EDGE,"E25.left")])]})]});
            var Q5;
            Q5=makeQuery(id+"F12.boolean.opBoolean","COPY",EDGE,{"derivedFrom":makeQuery(id+"F12.opExtrude","SWEPT_EDGE",EDGE,{"disambiguationData":[OSD([sQuery(id+"F8.wireOp",EDGE,"E25.top"),sQuery(id+"F8.wireOp",EDGE,"E25.left")])]})});
            var Q6;
            Q6=makeQuery(id+"F12.boolean.opBoolean","COPY",EDGE,{"derivedFrom":makeQuery(id+"F12.opExtrude","SWEPT_EDGE",EDGE,{"disambiguationData":[OSD([sQuery(id+"F8.wireOp",EDGE,"E25.top"),sQuery(id+"F8.wireOp",EDGE,"E25.right")])]})});
            var Q7;
            Q7=makeQuery(id+"F9.boolean.opBoolean","COPY",EDGE,{"derivedFrom":makeQuery(id+"F9.opExtrude","CAP_EDGE",EDGE,{"disambiguationData":[OSD([sQuery(id+"F0.wireOp",EDGE,"E6.bottom")])],"isStart":false})});
            var Q8;
            Q8=makeQuery(id+"F4.opExtrude","CAP_EDGE",EDGE,{"disambiguationData":[OSD([sQuery(id+"F0.wireOp",EDGE,"E3.left")])],"isStart":false});
            var Q9;
            Q9=makeQuery(id+"F4.opExtrude","CAP_EDGE",EDGE,{"disambiguationData":[OSD([sQuery(id+"F0.wireOp",EDGE,"E3.right")])],"isStart":false});
            fillet(context, id + "F14", {"entities" : qUnion([Q0, Q1, Q2, Q3, Q4, Q5, Q6, Q7, Q8, Q9]), "radius" : 2 * mm, "tangentPropagation" : true, "allowEdgeOverflow" : false});
        }
    });
